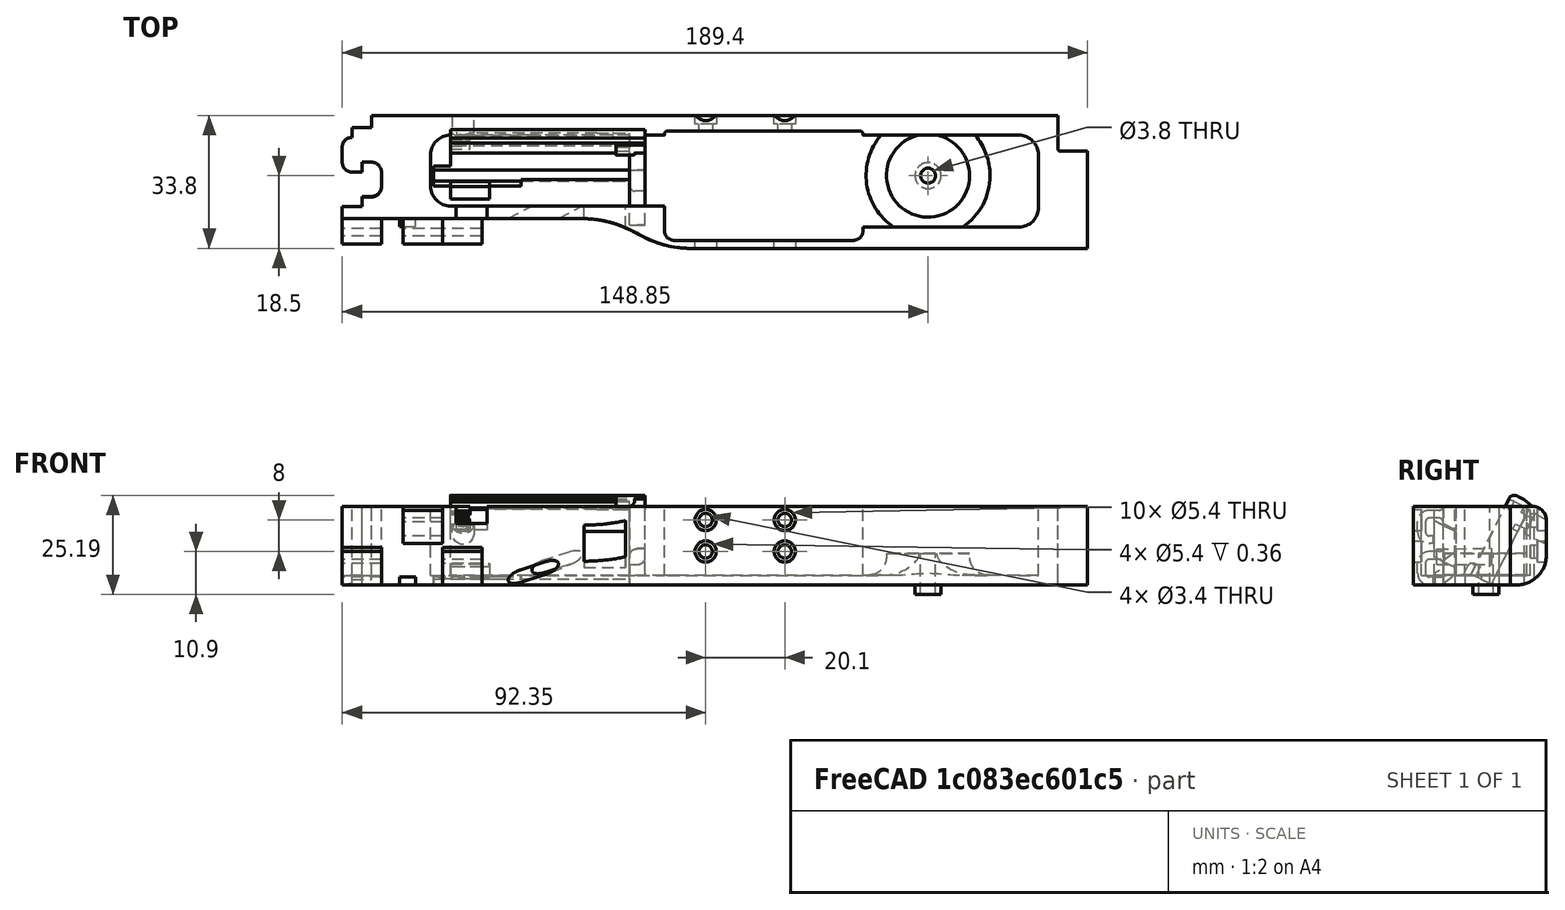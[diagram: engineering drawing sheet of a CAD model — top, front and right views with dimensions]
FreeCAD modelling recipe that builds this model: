
FCSTD DOCUMENT  (FreeCAD 0.19R0.19.2)
Label: v0_9993
License: All rights reserved
LicenseURL: http://en.wikipedia.org/wiki/All_rights_reserved
objects: Sketcher::SketchObject×44, Part::Extrusion×35, Part::MultiFuse×21, Part::Box×16, Part::Cut×15, Part::Fillet×13, App::MeasureDistance×6, Part::Cylinder×4, Part::Revolution×1, Mesh::Feature×1
note: 149 computed .brp shape members not serialized (recipe doc carries the construction recipe); baked Part::Feature solids carry a one-line shape summary decoded from their .brp

FEATURE [Sketcher::SketchObject] Sketch
  FullyConstrained = true
  sketch-geometry (36):
    g0: LineSegment StartX=0 StartY=0 StartZ=0 EndX=154.4 EndY=0 EndZ=0
    g1: LineSegment StartX=154.4 StartY=0 StartZ=0 EndX=154.4 EndY=-7.6 EndZ=0
    g2: LineSegment StartX=32.5209 StartY=-26.2 StartZ=0 EndX=-7.5 EndY=-26.2 EndZ=0
    g3-g7: Circle x5 (B-spline internal-alignment scaffolding for g8; pole/knot coordinates omitted)
    g8: BSplineCurve PolesCount=5 KnotsCount=3 Degree=3 IsPeriodic=0
    g9: GeomPoint X=61.85 Y=-33.8 Z=0
    g10: GeomPoint X=47.185 Y=-29.9 Z=0
    g11: GeomPoint X=32.5209 Y=-26.2 Z=0
    g12: Circle CenterX=121.35 CenterY=-14.3 CenterZ=0 NormalX=0 NormalY=0 NormalZ=1 AngleXU=0 Radius=3.25
    g13: LineSegment StartX=-7.5 StartY=-26.2 StartZ=0 EndX=-27.5 EndY=-26.2 EndZ=0
    g14: LineSegment StartX=-20 StartY=0 StartZ=0 EndX=0 EndY=0 EndZ=0
    g15: LineSegment StartX=-25 StartY=-3.1 StartZ=0 EndX=-20 EndY=-3.1 EndZ=0
    g16: LineSegment StartX=-25 StartY=-3.1 StartZ=0 EndX=-25 EndY=-5.6 EndZ=0
    g17: LineSegment StartX=-27.5 StartY=-8.1 StartZ=0 EndX=-27.5 EndY=-11.85 EndZ=0
    g18: ArcOfCircle CenterX=-25 CenterY=-8.1 CenterZ=0 NormalX=0 NormalY=0 NormalZ=1 AngleXU=0 Radius=2.5 StartAngle=1.5708 EndAngle=3.14159
    g19: LineSegment StartX=-25 StartY=-14.35 StartZ=0 EndX=-22.5 EndY=-14.35 EndZ=0
    g20: ArcOfCircle CenterX=-25 CenterY=-11.85 CenterZ=0 NormalX=0 NormalY=0 NormalZ=1 AngleXU=0 Radius=2.5 StartAngle=3.14159 EndAngle=4.71239
    g21: LineSegment StartX=-22.5 StartY=-14.35 StartZ=0 EndX=-22.5 EndY=-11.85 EndZ=0
    g22: LineSegment StartX=-22.5 StartY=-11.85 StartZ=0 EndX=-20 EndY=-11.85 EndZ=0
    g23: ArcOfCircle CenterX=-20 CenterY=-14.35 CenterZ=0 NormalX=0 NormalY=0 NormalZ=1 AngleXU=0 Radius=2.5 StartAngle=8e-16 EndAngle=1.5708
    g24: LineSegment StartX=-17.5 StartY=-14.35 StartZ=0 EndX=-17.5 EndY=-18.1 EndZ=0
    g25: ArcOfCircle CenterX=-20 CenterY=-18.1 CenterZ=0 NormalX=0 NormalY=0 NormalZ=1 AngleXU=0 Radius=2.5 StartAngle=4.71239 EndAngle=6.28319
    g26: LineSegment StartX=-22.5 StartY=-20.6 StartZ=0 EndX=-20 EndY=-20.6 EndZ=0
    g27: LineSegment StartX=-22.5 StartY=-20.6 StartZ=0 EndX=-22.5 EndY=-23.1 EndZ=0
    g28: LineSegment StartX=-27.5 StartY=-23.1 StartZ=0 EndX=-22.5 EndY=-23.1 EndZ=0
    g29: LineSegment StartX=-20 StartY=-3.1 StartZ=0 EndX=-20 EndY=0 EndZ=0
    g30: LineSegment StartX=-27.5 StartY=-23.1 StartZ=0 EndX=-27.5 EndY=-26.2 EndZ=0
    g31: LineSegment StartX=154.4 StartY=-7.6 StartZ=0 EndX=154.4 EndY=-8.6 EndZ=0
    g32: ArcOfCircle CenterX=154.9 CenterY=-8.6 CenterZ=0 NormalX=0 NormalY=0 NormalZ=1 AngleXU=0 Radius=0.5 StartAngle=3.14159 EndAngle=4.71239
    g33: LineSegment StartX=154.9 StartY=-9.1 StartZ=0 EndX=161.9 EndY=-9.1 EndZ=0
    g34: LineSegment StartX=161.9 StartY=-9.1 StartZ=0 EndX=161.9 EndY=-33.8 EndZ=0
    g35: LineSegment StartX=161.9 StartY=-33.8 StartZ=0 EndX=61.85 EndY=-33.8 EndZ=0
  constraints (72):
    c: PointOnObject(g0,g-2)
    c: Horizontal(g0)
    c: Distance(g0) = 154.4
    c: DistanceY(g-1,g0) = 0
    c: Vertical(g1)
    c: Distance(g1) = 7.6
    c: Coincident(g1,g0)
    c: Horizontal(g2)
    c: Block(g2)
    c: Weight(g3) = 1
    c: Coincident(g8,g2)
    c: InternalAlignment(g3-g7 -> g8) x5
    c: InternalAlignment(g9,g8)
    c: InternalAlignment(g10,g8)
    c: InternalAlignment(g11,g8)
    c: Block(g12)
    c: Coincident(g13,g2)
    c: Horizontal(g13)
    c: Distance(g13) = 20
    c: Horizontal(g14)
    c: Distance(g14) = 20
    c: Coincident(g14,g0)
    c: Horizontal(g15)
    c: Vertical(g16)
    c: Coincident(g16,g15)
    c: Vertical(g17)
    c: Coincident(g18,g16)
    c: Block(g18)
    c: Coincident(g17,g18)
    c: Horizontal(g19)
    c: Coincident(g20,g17)
    c: Block(g20)
    c: Block(g19)
    c: Vertical(g21)
    c: Coincident(g21,g19)
    c: Horizontal(g22)
    c: Coincident(g22,g21)
    c: Coincident(g23,g22)
    c: Vertical(g24)
    c: Block(g23)
    c: Coincident(g24,g23)
    c: Coincident(g25,g24)
    c: Block(g25)
    c: Horizontal(g26)
    c: Coincident(g26,g25)
    c: Vertical(g27)
    c: Coincident(g27,g26)
    c: Horizontal(g28)
    c: Coincident(g28,g27)
    c: Block(g15)
    c: Block(g28)
    c: Coincident(g29,g15)
    c: Coincident(g29,g14)
    c: Vertical(g29)
    c: Coincident(g30,g28)
    c: Coincident(g30,g13)
    c: Vertical(g30)
    c: Vertical(g31)
    c: Distance(g31) = 1
    c: Coincident(g31,g1)
    c: Coincident(g32,g31)
    c: Block(g32)
    c: Coincident(g33,g32)
    c: Horizontal(g33)
    c: Coincident(g34,g33)
    c: Vertical(g34)
    c: Block(g34)
    c: Coincident(g35,g34)
    c: Horizontal(g35)
    c: Block(g35)
    c: Coincident(g8,g35)
    c: Block(g8)
FEATURE [Part::Extrusion] Extrude  label="mainBodyBaseExtrude"
  Base = -> Sketch
  Dir = (0,0,1)
  DirMode = 2
  FaceMakerClass = Part::FaceMakerBullseye
  LengthFwd = 2.4
  LengthRev = 0
  Solid = true
  Symmetric = false
FEATURE [Sketcher::SketchObject] Sketch001
  FullyConstrained = true
  sketch-geometry (75):
    g0: ArcOfCircle CenterX=144.4 CenterY=-10 CenterZ=0 NormalX=0 NormalY=0 NormalZ=1 AngleXU=0 Radius=5 StartAngle=4.345e-13 EndAngle=1.5708
    g1: LineSegment StartX=32.5209 StartY=-26.2 StartZ=0 EndX=-7.49911 EndY=-26.2 EndZ=0
    g2: LineSegment StartX=0 StartY=0 StartZ=0 EndX=154.4 EndY=0 EndZ=0
    g3-g7: Circle x5 (B-spline internal-alignment scaffolding for g8; pole/knot coordinates omitted)
    g8: BSplineCurve PolesCount=5 KnotsCount=3 Degree=3 IsPeriodic=0
    g9: GeomPoint X=61.85 Y=-33.8 Z=0
    g10: GeomPoint X=47.1857 Y=-29.9 Z=0
    g11: GeomPoint X=32.5209 Y=-26.2 Z=0
    g12: LineSegment StartX=154.4 StartY=0 StartZ=0 EndX=154.4 EndY=-7.6 EndZ=0
    g13: LineSegment StartX=20 StartY=-5 StartZ=0 EndX=54.35 EndY=-5 EndZ=0
    g14: LineSegment StartX=104.85 StartY=-5 StartZ=0 EndX=144.4 EndY=-5 EndZ=0
    g15: LineSegment StartX=54.35 StartY=-23 StartZ=0 EndX=20 EndY=-23 EndZ=0
    g16: LineSegment StartX=-27.4991 StartY=-26.2 StartZ=0 EndX=-7.49911 EndY=-26.2 EndZ=0
    g17: LineSegment StartX=-20 StartY=0 StartZ=0 EndX=0 EndY=0 EndZ=0
    g18: LineSegment StartX=-27.4991 StartY=-23.2 StartZ=0 EndX=-22.5 EndY=-23.2 EndZ=0
    g19: LineSegment StartX=-22.5 StartY=-20.7 StartZ=0 EndX=-22.5 EndY=-23.2 EndZ=0
    g20: LineSegment StartX=-22.5 StartY=-20.7 StartZ=0 EndX=-20 EndY=-20.7 EndZ=0
    g21: ArcOfCircle CenterX=-20 CenterY=-18.2 CenterZ=0 NormalX=0 NormalY=0 NormalZ=1 AngleXU=0 Radius=2.5 StartAngle=4.71239 EndAngle=6.28319
    g22: LineSegment StartX=-17.5 StartY=-14.4 StartZ=0 EndX=-17.5 EndY=-18.2 EndZ=0
    g23: ArcOfCircle CenterX=-20 CenterY=-14.4 CenterZ=0 NormalX=0 NormalY=0 NormalZ=1 AngleXU=0 Radius=2.5 StartAngle=9e-16 EndAngle=1.5708
    g24: LineSegment StartX=-22.5 StartY=-11.9 StartZ=0 EndX=-20 EndY=-11.9 EndZ=0
    g25: LineSegment StartX=-22.5 StartY=-14.4 StartZ=0 EndX=-22.5 EndY=-11.9 EndZ=0
    g26: LineSegment StartX=-25 StartY=-14.4 StartZ=0 EndX=-22.5 EndY=-14.4 EndZ=0
    g27: ArcOfCircle CenterX=-25 CenterY=-11.9 CenterZ=0 NormalX=0 NormalY=0 NormalZ=1 AngleXU=0 Radius=2.5 StartAngle=3.14159 EndAngle=4.71239
    g28: LineSegment StartX=-27.5 StartY=-8.1 StartZ=0 EndX=-27.5 EndY=-11.9 EndZ=0
    g29: ArcOfCircle CenterX=-25 CenterY=-8.1 CenterZ=0 NormalX=0 NormalY=0 NormalZ=1 AngleXU=0 Radius=2.5 StartAngle=1.5708 EndAngle=3.14159
    g30: LineSegment StartX=-25 StartY=-3.1 StartZ=0 EndX=-25 EndY=-5.6 EndZ=0
    g31: LineSegment StartX=-20 StartY=-3.1 StartZ=0 EndX=-25 EndY=-3.1 EndZ=0
    g32: LineSegment StartX=-20 StartY=0 StartZ=0 EndX=-20 EndY=-3.1 EndZ=0
    g33: LineSegment StartX=-27.4991 StartY=-26.2 StartZ=0 EndX=-27.4991 EndY=-23.2 EndZ=0
    g34: LineSegment StartX=4.09e-14 StartY=-5 StartZ=0 EndX=20 EndY=-5 EndZ=0
    g35: ArcOfCircle CenterX=7.1e-15 CenterY=-18 CenterZ=0 NormalX=0 NormalY=0 NormalZ=1 AngleXU=0 Radius=5 StartAngle=3.14159 EndAngle=4.71239
    g36: ArcOfCircle CenterX=4.26e-14 CenterY=-10 CenterZ=0 NormalX=0 NormalY=0 NormalZ=1 AngleXU=0 Radius=5 StartAngle=1.5708 EndAngle=3.14159
    g37: LineSegment StartX=-5 StartY=-18 StartZ=0 EndX=-5 EndY=-10 EndZ=0
    g38: LineSegment StartX=6.2e-15 StartY=-23 StartZ=0 EndX=20 EndY=-23 EndZ=0
    g39: LineSegment StartX=154.4 StartY=-7.6 StartZ=0 EndX=154.4 EndY=-8.6 EndZ=0
    g40: LineSegment StartX=154.9 StartY=-9.1 StartZ=0 EndX=161.9 EndY=-9.1 EndZ=0
    g41: ArcOfCircle CenterX=154.9 CenterY=-8.6 CenterZ=0 NormalX=0 NormalY=0 NormalZ=1 AngleXU=0 Radius=0.5 StartAngle=3.14159 EndAngle=4.71299
    g42: LineSegment StartX=104.85 StartY=-28.3916 StartZ=0 EndX=144.408 EndY=-28.3916 EndZ=0
    g43: LineSegment StartX=149.4 StartY=-10 StartZ=0 EndX=149.4 EndY=-23.4 EndZ=0
    g44: ArcOfCircle CenterX=144.408 CenterY=-23.4 CenterZ=0 NormalX=0 NormalY=0 NormalZ=1 AngleXU=0 Radius=4.99164 StartAngle=4.71239 EndAngle=6.28319
    g45: LineSegment StartX=104.85 StartY=-28.3916 StartZ=0 EndX=104.85 EndY=-28.7833 EndZ=0
    g46: LineSegment StartX=54.35 StartY=-28.7916 StartZ=0 EndX=54.35 EndY=-23 EndZ=0
    g47: LineSegment StartX=161.9 StartY=-33.8 StartZ=0 EndX=161.9 EndY=-9.1 EndZ=0
    g48: LineSegment StartX=61.85 StartY=-33.8 StartZ=0 EndX=161.9 EndY=-33.8 EndZ=0
    g49: Circle CenterX=54.35 CenterY=-28.7916 CenterZ=0 NormalX=0 NormalY=0 NormalZ=1 AngleXU=0 Radius=1
    g50: Circle CenterX=54.35 CenterY=-31.7916 CenterZ=0 NormalX=0 NormalY=0 NormalZ=1 AngleXU=0 Radius=1
    g51: Circle CenterX=57.35 CenterY=-31.7916 CenterZ=0 NormalX=0 NormalY=0 NormalZ=1 AngleXU=0 Radius=1
    g52: BSplineCurve PolesCount=3 KnotsCount=2 Degree=2 IsPeriodic=0
    g53: GeomPoint X=54.35 Y=-28.7916 Z=0
    g54: GeomPoint X=57.35 Y=-31.7916 Z=0
    g55: Circle CenterX=104.85 CenterY=-28.7833 CenterZ=0 NormalX=0 NormalY=0 NormalZ=1 AngleXU=0 Radius=1
    g56: Circle CenterX=104.85 CenterY=-31.7916 CenterZ=0 NormalX=0 NormalY=0 NormalZ=1 AngleXU=0 Radius=1
    g57: Circle CenterX=101.85 CenterY=-31.7916 CenterZ=0 NormalX=0 NormalY=0 NormalZ=1 AngleXU=0 Radius=1
    g58: BSplineCurve PolesCount=3 KnotsCount=2 Degree=2 IsPeriodic=0
    g59: GeomPoint X=104.85 Y=-28.7833 Z=0
    g60: GeomPoint X=101.85 Y=-31.7916 Z=0
    g61: LineSegment StartX=57.35 StartY=-31.7916 StartZ=0 EndX=101.85 EndY=-31.7916 EndZ=0
    g62: Circle CenterX=54.35 CenterY=-5 CenterZ=0 NormalX=0 NormalY=0 NormalZ=1 AngleXU=0 Radius=1
    g63: Circle CenterX=54.35 CenterY=-4 CenterZ=0 NormalX=0 NormalY=0 NormalZ=1 AngleXU=0 Radius=1
    g64: Circle CenterX=55.15 CenterY=-4 CenterZ=0 NormalX=0 NormalY=0 NormalZ=1 AngleXU=0 Radius=1
    g65: BSplineCurve PolesCount=3 KnotsCount=2 Degree=2 IsPeriodic=0
    g66: GeomPoint X=54.35 Y=-5 Z=0
    g67: GeomPoint X=55.15 Y=-4 Z=0
    g68: Circle CenterX=104.85 CenterY=-5 CenterZ=0 NormalX=0 NormalY=0 NormalZ=1 AngleXU=0 Radius=1
    g69: Circle CenterX=104.85 CenterY=-4 CenterZ=0 NormalX=0 NormalY=0 NormalZ=1 AngleXU=0 Radius=1
    g70: Circle CenterX=104.05 CenterY=-4 CenterZ=0 NormalX=0 NormalY=0 NormalZ=1 AngleXU=0 Radius=1
    g71: BSplineCurve PolesCount=3 KnotsCount=2 Degree=2 IsPeriodic=0
    g72: GeomPoint X=104.85 Y=-5 Z=0
    g73: GeomPoint X=104.05 Y=-4 Z=0
    g74: LineSegment StartX=104.05 StartY=-4 StartZ=0 EndX=55.15 EndY=-4 EndZ=0
  constraints (156):
    c: PointOnObject(g2,g-2)
    c: DistanceY(g-1,g2) = 0
    c: Block(g0)
    c: Horizontal(g1)
    c: Distance(g1) = 40.02
    c: Horizontal(g2)
    c: Block(g2)
    c: Weight(g3) = 1
    c: Equal(g3, g4-g7) x4
    c: Coincident(g8,g1)
    c: InternalAlignment(g3-g7 -> g8) x5
    c: InternalAlignment(g9,g8)
    c: InternalAlignment(g10,g8)
    c: InternalAlignment(g11,g8)
    c: Vertical(g12)
    c: Coincident(g12,g2)
    c: Distance(g12) = 7.6
    c: Block(g12)
    c: Horizontal(g13)
    c: Coincident(g14,g0)
    c: Horizontal(g14)
    c: Horizontal(g15)
    c: Horizontal(g16)
    c: Distance(g16) = 20
    c: Coincident(g1,g16)
    c: Horizontal(g17)
    c: Distance(g17) = 20
    c: Coincident(g17,g2)
    c: Horizontal(g31)
    c: Vertical(g30)
    c: Coincident(g29,g30)
    c: Vertical(g28)
    c: Block(g29)
    c: Coincident(g27,g28)
    c: Block(g27)
    c: Horizontal(g26)
    c: Coincident(g26,g27)
    c: Vertical(g25)
    c: Coincident(g25,g26)
    c: Horizontal(g24)
    c: Coincident(g23,g24)
    c: Block(g23)
    c: Vertical(g22)
    c: Coincident(g21,g22)
    c: Block(g21)
    c: Horizontal(g20)
    c: Coincident(g20,g21)
    c: Vertical(g19)
    c: Coincident(g19,g20)
    c: Horizontal(g18)
    c: Coincident(g18,g19)
    c: Coincident(g32,g17)
    c: Coincident(g32,g31)
    c: Vertical(g32)
    c: Coincident(g33,g16)
    c: Coincident(g33,g18)
    c: Vertical(g33)
    c: Block(g33)
    c: Block(g18)
    c: Block(g22)
    c: Block(g26)
    c: Block(g25)
    c: Block(g24)
    c: Block(g28)
    c: Block(g31)
    c: Block(g30)
    c: Horizontal(g34)
    c: Distance(g34) = 20
    c: Block(g35)
    c: Block(g36)
    c: Coincident(g37,g35)
    c: Coincident(g37,g36)
    c: Vertical(g37)
    c: Coincident(g38,g35)
    c: Coincident(g38,g15)
    c: Horizontal(g38)
    c: Block(g38)
    c: Block(g34)
    c: Block(g13)
    c: Vertical(g39)
    c: Distance(g39) = 1
    c: Coincident(g39,g12)
    c: Horizontal(g40)
    c: Coincident(g41,g39)
    c: Coincident(g41,g40)
    c: Block(g39)
    c: Block(g41)
    c: Horizontal(g42)
    c: Vertical(g43)
    c: Distance(g43) = 13.4
    c: Coincident(g43,g0)
    c: Block(g42)
    c: Block(g43)
    c: Coincident(g44,g43)
    c: Coincident(g44,g42)
    c: Block(g44)
    c: Distance(g15) = 34.35
    c: Coincident(g45,g42)
    c: Vertical(g45)
    c: Coincident(g46,g15)
    c: Vertical(g46)
    c: Coincident(g47,g40)
    c: Vertical(g47)
    c: Block(g47)
    c: Coincident(g48,g47)
    c: Horizontal(g48)
    c: Block(g48)
    c: Coincident(g8,g48)
    c: Block(g8)
    c: Coincident(g52,g46)
    c: Weight(g49) = 1
    c: Equal(g49,g50)
    c: Equal(g49,g51)
    c: InternalAlignment(g49,g52)
    c: InternalAlignment(g50,g52)
    c: InternalAlignment(g51,g52)
    c: InternalAlignment(g53,g52)
    c: InternalAlignment(g54,g52)
    c: Coincident(g58,g45)
    c: Weight(g55) = 1
    c: Equal(g55,g56)
    c: Equal(g55,g57)
    c: InternalAlignment(g55,g58)
    c: InternalAlignment(g56,g58)
    c: InternalAlignment(g57,g58)
    c: InternalAlignment(g59,g58)
    c: InternalAlignment(g60,g58)
    c: Block(g58)
    c: Block(g52)
    c: Coincident(g61,g52)
    c: Coincident(g61,g58)
    c: Horizontal(g61)
    c: Block(g14)
    c: Coincident(g65,g13)
    c: Weight(g62) = 1
    c: Equal(g62,g63)
    c: Equal(g62,g64)
    c: InternalAlignment(g62,g65)
    c: InternalAlignment(g63,g65)
    c: InternalAlignment(g64,g65)
    c: InternalAlignment(g66,g65)
    c: InternalAlignment(g67,g65)
    c: Block(g65)
    c: Coincident(g71,g14)
    c: Weight(g68) = 1
    c: Equal(g68,g69)
    c: Equal(g68,g70)
    c: InternalAlignment(g68,g71)
    c: InternalAlignment(g69,g71)
    c: InternalAlignment(g70,g71)
    c: InternalAlignment(g72,g71)
    c: InternalAlignment(g73,g71)
    c: Block(g71)
    c: Coincident(g74,g71)
    c: Coincident(g74,g65)
    c: Horizontal(g74)
FEATURE [Sketcher::SketchObject] Sketch005
  FullyConstrained = true
  Placement = pos=(0,0,0) rot=(1,0,0;1.5708rad)
  sketch-geometry (4):
    g0: Circle CenterX=84.95 CenterY=16.5 CenterZ=0 NormalX=0 NormalY=0 NormalZ=1 AngleXU=0 Radius=1.7
    g1: Circle CenterX=84.95 CenterY=8.5 CenterZ=0 NormalX=0 NormalY=0 NormalZ=1 AngleXU=0 Radius=1.7
    g2: Circle CenterX=64.85 CenterY=8.5 CenterZ=0 NormalX=0 NormalY=0 NormalZ=1 AngleXU=0 Radius=1.7
    g3: Circle CenterX=64.85 CenterY=16.5 CenterZ=0 NormalX=0 NormalY=0 NormalZ=1 AngleXU=0 Radius=1.7
  constraints (4):
    c: Block(g0)
    c: Block(g1)
    c: Block(g2)
    c: Block(g3)
FEATURE [Part::Extrusion] Extrude004  label="removeFromMainBodyToCreateScrewHolesForSolenoidExtrude004"
  Base = -> Sketch005
  Dir = (0,-1,1.1e-15)
  DirMode = 2
  FaceMakerClass = Part::FaceMakerBullseye
  LengthFwd = 10
  LengthRev = 0
  Solid = true
  Symmetric = false
FEATURE [Sketcher::SketchObject] Sketch004
  FullyConstrained = true
  Placement = pos=(0,0,0) rot=(1,0,0;1.5708rad)
  sketch-geometry (12):
    g0: LineSegment StartX=15.75 StartY=2.5 StartZ=0 EndX=15.75 EndY=0 EndZ=0
    g1: Circle CenterX=15.75 CenterY=2.5 CenterZ=0 NormalX=0 NormalY=0 NormalZ=1 AngleXU=0 Radius=1
    g2: Circle CenterX=10.55 CenterY=2.5 CenterZ=0 NormalX=0 NormalY=0 NormalZ=1 AngleXU=0 Radius=1
    g3: Circle CenterX=10.55 CenterY=8 CenterZ=0 NormalX=0 NormalY=0 NormalZ=1 AngleXU=0 Radius=1
    g4: BSplineCurve PolesCount=3 KnotsCount=2 Degree=2 IsPeriodic=0
    g5: GeomPoint X=15.75 Y=2.5 Z=0
    g6: GeomPoint X=10.55 Y=8 Z=0
    g7: LineSegment StartX=1.9 StartY=8 StartZ=0 EndX=10.55 EndY=8 EndZ=0
    g8: LineSegment StartX=1.9 StartY=-2.4 StartZ=0 EndX=1.9 EndY=8 EndZ=0
    g9: LineSegment StartX=3.30092 StartY=-2.4 StartZ=0 EndX=3.30092 EndY=0 EndZ=0
    g10: LineSegment StartX=15.75 StartY=0 StartZ=0 EndX=3.30092 EndY=0 EndZ=0
    g11: LineSegment StartX=3.30092 StartY=-2.4 StartZ=0 EndX=1.9 EndY=-2.4 EndZ=0
  constraints (26):
    c: Vertical(g0)
    c: Distance(g0) = 2.5
    c: Coincident(g4,g0)
    c: Weight(g1) = 1
    c: Equal(g1,g2)
    c: Equal(g1,g3)
    c: InternalAlignment(g1,g4)
    c: InternalAlignment(g2,g4)
    c: InternalAlignment(g3,g4)
    c: InternalAlignment(g5,g4)
    c: InternalAlignment(g6,g4)
    c: Block(g4)
    c: Coincident(g7,g4)
    c: Horizontal(g7)
    c: Vertical(g8)
    c: Coincident(g8,g7)
    c: Block(g8)
    c: Vertical(g9)
    c: Coincident(g10,g0)
    c: PointOnObject(g10,g-1)
    c: Horizontal(g10)
    c: Coincident(g10,g9)
    c: Block(g9)
    c: Coincident(g11,g9)
    c: Coincident(g11,g8)
    c: Horizontal(g11)
FEATURE [Sketcher::SketchObject] Sketch007
  FullyConstrained = true
  Placement = pos=(0,-14.3,2.37) rot=(-1,0,0;2.03453rad)
  sketch-geometry (6):
    g0: LineSegment StartX=0 StartY=0 StartZ=0 EndX=45.5 EndY=0 EndZ=0
    g1: LineSegment StartX=0 StartY=0 StartZ=0 EndX=0 EndY=-21.2 EndZ=0
    g2: LineSegment StartX=45.5 StartY=0 StartZ=0 EndX=49.5 EndY=0 EndZ=0
    g3: LineSegment StartX=49.5 StartY=0 StartZ=0 EndX=49.5 EndY=-21.2 EndZ=0
    g4: LineSegment StartX=49.5 StartY=-21.2 StartZ=0 EndX=0 EndY=-21.2 EndZ=0
    g5: Circle CenterX=3.25 CenterY=-18.05 CenterZ=0 NormalX=0 NormalY=0 NormalZ=1 AngleXU=0 Radius=1.6
  constraints (15):
    c: Coincident(g0,g-1)
    c: Horizontal(g0)
    c: Distance(g0) = 45.5
    c: Coincident(g1,g0)
    c: Vertical(g1)
    c: Horizontal(g2)
    c: Distance(g2) = 4
    c: Coincident(g2,g0)
    c: Coincident(g3,g2)
    c: Vertical(g3)
    c: Block(g3)
    c: Coincident(g4,g3)
    c: Horizontal(g4)
    c: Coincident(g4,g1)
    c: Block(g5)
FEATURE [Part::Extrusion] Extrude005  label="solenoidDriverHolderExtrude005"
  Base = -> Sketch007
  Dir = (0,0.894389,-0.447291)
  DirMode = 2
  FaceMakerClass = Part::FaceMakerBullseye
  LengthFwd = 10
  LengthRev = 0
  Placement = pos=(0,0,-2) rot=(0,0,1;0rad)
  Solid = true
  Symmetric = false
FEATURE [Sketcher::SketchObject] Sketch008
  FullyConstrained = false
  Placement = pos=(0,-4.3,-2.6) rot=(-1,0,0;2.03453rad)
  sketch-geometry (1):
    g0: Circle CenterX=42.25 CenterY=-3.15 CenterZ=0 NormalX=0 NormalY=0 NormalZ=1 AngleXU=0 Radius=4.5
FEATURE [Sketcher::SketchObject] Sketch009
  FullyConstrained = true
  Placement = pos=(0,-4.3,-2.6) rot=(-1,0,0;2.03453rad)
  sketch-geometry (1):
    g0: Circle CenterX=3.25 CenterY=-18.0217 CenterZ=0 NormalX=0 NormalY=0 NormalZ=1 AngleXU=0 Radius=2.8
  constraints (1):
    c: Block(g0)
FEATURE [Sketcher::SketchObject] Sketch010
  FullyConstrained = true
  Placement = pos=(0,-14.3,2.37) rot=(-1,0,0;2.03453rad)
  sketch-geometry (1):
    g0: Circle CenterX=3.25 CenterY=-18.05 CenterZ=0 NormalX=0 NormalY=0 NormalZ=1 AngleXU=0 Radius=1.6
  constraints (1):
    c: Block(g0)
FEATURE [Part::Extrusion] Extrude008  label="removeFromScrewHole3"
  Base = -> Sketch010
  Dir = (0,0.894389,-0.447291)
  DirMode = 2
  FaceMakerClass = Part::FaceMakerBullseye
  LengthFwd = -25
  LengthRev = 0
  Placement = pos=(0,4,-4) rot=(0,0,1;0rad)
  Solid = true
  Symmetric = false
FEATURE [Sketcher::SketchObject] Sketch011
  FullyConstrained = true
  Placement = pos=(0,-14.3,2.37) rot=(-1,0,0;2.03453rad)
  sketch-geometry (4):
    g0: LineSegment StartX=49.5 StartY=-21.2 StartZ=0 EndX=49.5 EndY=-22.8 EndZ=0
    g1: LineSegment StartX=49.5 StartY=-22.8 StartZ=0 EndX=0.002238 EndY=-22.8 EndZ=0
    g2: LineSegment StartX=0.002238 StartY=-21.2 StartZ=0 EndX=0.002238 EndY=-22.8 EndZ=0
    g3: LineSegment StartX=49.5 StartY=-21.2 StartZ=0 EndX=0.002238 EndY=-21.2 EndZ=0
  constraints (10):
    c: Vertical(g0)
    c: Distance(g0) = 1.6
    c: Coincident(g1,g0)
    c: Horizontal(g1)
    c: Vertical(g2)
    c: Coincident(g2,g1)
    c: Coincident(g3,g0)
    c: Coincident(g3,g2)
    c: Horizontal(g3)
    c: Block(g3)
FEATURE [Part::Extrusion] Extrude009  label="solenoidDriverTopLipFront"
  Base = -> Sketch011
  Dir = (0,0.894389,-0.447291)
  DirMode = 2
  FaceMakerClass = Part::FaceMakerBullseye
  LengthFwd = -2
  LengthRev = 0
  Placement = pos=(0,-2.9,-0.35) rot=(0,0,1;0rad)
  Solid = true
  Symmetric = false
FEATURE [Sketcher::SketchObject] Sketch012
  FullyConstrained = true
  Placement = pos=(0,-14.3,2.37) rot=(-1,0,0;2.03453rad)
  sketch-geometry (4):
    g0: LineSegment StartX=49.5 StartY=-21.2 StartZ=0 EndX=49.5 EndY=-22.8 EndZ=0
    g1: LineSegment StartX=49.5 StartY=-22.8 StartZ=0 EndX=0.002238 EndY=-22.8 EndZ=0
    g2: LineSegment StartX=0.002238 StartY=-21.2 StartZ=0 EndX=0.002238 EndY=-22.8 EndZ=0
    g3: LineSegment StartX=49.5 StartY=-21.2 StartZ=0 EndX=0.002238 EndY=-21.2 EndZ=0
  constraints (10):
    c: Vertical(g0)
    c: Distance(g0) = 1.6
    c: Coincident(g1,g0)
    c: Horizontal(g1)
    c: Vertical(g2)
    c: Coincident(g2,g1)
    c: Coincident(g3,g0)
    c: Coincident(g3,g2)
    c: Horizontal(g3)
    c: Block(g3)
FEATURE [Part::Extrusion] Extrude010  label="solenoidDriverTopLipLowerExtrude010"
  Base = -> Sketch012
  Dir = (0,0.894389,-0.447291)
  DirMode = 2
  FaceMakerClass = Part::FaceMakerBullseye
  LengthFwd = 5.05
  LengthRev = 0
  Solid = true
  Symmetric = false
FEATURE [Sketcher::SketchObject] Sketch015
  FullyConstrained = true
  Placement = pos=(0,-14.3,2.37) rot=(-1,0,0;2.03453rad)
  sketch-geometry (4):
    g0: LineSegment StartX=0 StartY=1.5 StartZ=0 EndX=0 EndY=0 EndZ=0
    g1: LineSegment StartX=0 StartY=1.5 StartZ=0 EndX=5 EndY=1.5 EndZ=0
    g2: LineSegment StartX=5 StartY=1.5 StartZ=0 EndX=5 EndY=0 EndZ=0
    g3: LineSegment StartX=0 StartY=0 StartZ=0 EndX=5 EndY=0 EndZ=0
  constraints (13):
    c: Vertical(g0)
    c: Distance(g0) = 1.5
    c: Horizontal(g1)
    c: Distance(g1) = 5
    c: Coincident(g1,g0)
    c: Vertical(g2)
    c: Distance(g2) = 1.5
    c: Coincident(g2,g1)
    c: Block(g1)
    c: Block(g2)
    c: Block(g0)
    c: Coincident(g3,g0)
    c: Coincident(g3,g2)
FEATURE [Part::Extrusion] Extrude013  label="solenoidDriverBottomLipTopExtrude012"
  Base = -> Sketch015
  Dir = (0,0.894389,-0.447291)
  DirMode = 2
  FaceMakerClass = Part::FaceMakerBullseye
  LengthFwd = -6.5
  LengthRev = 0
  Placement = pos=(0,-14.15,19.65) rot=(1,0,0;1.5708rad)
  Solid = true
  Symmetric = false
FEATURE [Sketcher::SketchObject] Sketch016
  FullyConstrained = true
  Placement = pos=(0,0,0) rot=(1,0,0;1.5708rad)
  sketch-geometry (4):
    g0: Circle CenterX=84.15 CenterY=16.5 CenterZ=0 NormalX=0 NormalY=0 NormalZ=1 AngleXU=0 Radius=2.7
    g1: Circle CenterX=64.05 CenterY=16.5 CenterZ=0 NormalX=0 NormalY=0 NormalZ=1 AngleXU=0 Radius=2.7
    g2: Circle CenterX=64.05 CenterY=8.5 CenterZ=0 NormalX=0 NormalY=0 NormalZ=1 AngleXU=0 Radius=2.7
    g3: Circle CenterX=84.15 CenterY=8.5 CenterZ=0 NormalX=0 NormalY=0 NormalZ=1 AngleXU=0 Radius=2.7
  constraints (4):
    c: Block(g0)
    c: Block(g1)
    c: Block(g3)
    c: Block(g2)
FEATURE [Part::Extrusion] Extrude014  label="removeFromMainBodyToCreateScrewHoleCounterSinks"
  Base = -> Sketch016
  Dir = (0,-1,1.1e-15)
  DirMode = 2
  FaceMakerClass = Part::FaceMakerBullseye
  LengthFwd = 1.9
  LengthRev = 0
  Placement = pos=(0.8,-0.36,0) rot=(0,0,1;0rad)
  Solid = true
  Symmetric = false
FEATURE [Part::Extrusion] Extrude015  label="removeFromScrewHole2Extrude007"
  Base = -> Sketch009
  Dir = (0,0.894389,-0.447291)
  DirMode = 2
  FaceMakerClass = Part::FaceMakerBullseye
  LengthFwd = 10
  LengthRev = 0
  Placement = pos=(0,-8,2) rot=(0,0,1;0rad)
  Solid = true
  Symmetric = false
FEATURE [Sketcher::SketchObject] Sketch017
  FullyConstrained = true
  Placement = pos=(0,-14.3,2.37) rot=(-1,0,0;2.03453rad)
  sketch-geometry (4):
    g0: LineSegment StartX=0 StartY=1.5 StartZ=0 EndX=0 EndY=0 EndZ=0
    g1: LineSegment StartX=0 StartY=1.5 StartZ=0 EndX=5 EndY=1.5 EndZ=0
    g2: LineSegment StartX=5 StartY=1.5 StartZ=0 EndX=5 EndY=0 EndZ=0
    g3: LineSegment StartX=0 StartY=0 StartZ=0 EndX=5 EndY=0 EndZ=0
  constraints (13):
    c: Vertical(g0)
    c: Distance(g0) = 1.5
    c: Horizontal(g1)
    c: Distance(g1) = 5
    c: Coincident(g1,g0)
    c: Vertical(g2)
    c: Distance(g2) = 1.5
    c: Coincident(g2,g1)
    c: Block(g1)
    c: Block(g2)
    c: Block(g0)
    c: Coincident(g3,g0)
    c: Coincident(g3,g2)
FEATURE [Part::Extrusion] Extrude016  label="solenoidDriverBottomLipTopExtrude013"
  Base = -> Sketch017
  Dir = (0,0.894389,-0.447291)
  DirMode = 2
  FaceMakerClass = Part::FaceMakerBullseye
  LengthFwd = -6.5
  LengthRev = 0
  Placement = pos=(0,-15.45,20.3) rot=(1,0,0;1.5708rad)
  Solid = true
  Symmetric = false
FEATURE [Part::Fillet] Fillet005  label="solenoidDriverBottomLipTopFillet005"
  Base = -> Extrude016
  Edges = 1 edges r=1.4: [Edge6]
FEATURE [Sketcher::SketchObject] Sketch018
  FullyConstrained = true
  Placement = pos=(38.5,-14.3,2.37) rot=(-1,0,0;2.03453rad)
  sketch-geometry (4):
    g0: LineSegment StartX=11 StartY=0 StartZ=0 EndX=11 EndY=1.5 EndZ=0
    g1: LineSegment StartX=11 StartY=0 StartZ=0 EndX=3.6 EndY=0 EndZ=0
    g2: LineSegment StartX=3.6 StartY=0 StartZ=0 EndX=3.6 EndY=1.5 EndZ=0
    g3: LineSegment StartX=11 StartY=1.5 StartZ=0 EndX=3.6 EndY=1.5 EndZ=0
  constraints (12):
    c: PointOnObject(g0,g-1)
    c: Vertical(g0)
    c: Distance(g0) = 1.5
    c: Horizontal(g1)
    c: Distance(g1) = 7.4
    c: Coincident(g1,g0)
    c: Block(g0)
    c: Coincident(g2,g1)
    c: Vertical(g2)
    c: Coincident(g3,g0)
    c: Horizontal(g3)
    c: Coincident(g2,g3)
FEATURE [Part::Extrusion] Extrude017
  Base = -> Sketch018
  Dir = (0,0.894389,-0.447291)
  DirMode = 2
  FaceMakerClass = Part::FaceMakerBullseye
  LengthFwd = 4
  LengthRev = 0
  Placement = pos=(0,-8.212,34.025) rot=(1,0,0;1.5708rad)
  Solid = true
  Symmetric = false
FEATURE [Sketcher::SketchObject] Sketch019
  FullyConstrained = true
  Placement = pos=(0,0,0) rot=(1,0,0;1.5708rad)
  sketch-geometry (4):
    g0: Circle CenterX=84.95 CenterY=8.5 CenterZ=0 NormalX=0 NormalY=0 NormalZ=1 AngleXU=0 Radius=2.7
    g1: Circle CenterX=64.85 CenterY=8.5 CenterZ=0 NormalX=0 NormalY=0 NormalZ=1 AngleXU=0 Radius=2.7
    g2: Circle CenterX=64.85 CenterY=16.5 CenterZ=0 NormalX=0 NormalY=0 NormalZ=1 AngleXU=0 Radius=2.7
    g3: Circle CenterX=84.95 CenterY=16.5 CenterZ=0 NormalX=0 NormalY=0 NormalZ=1 AngleXU=0 Radius=2.7
  constraints (4):
    c: Block(g3)
    c: Block(g2)
    c: Block(g0)
    c: Block(g1)
FEATURE [Part::Extrusion] Extrude019  label="removeSolenoidAdjusterHoles"
  Base = -> Sketch019
  Dir = (0,-1,1.1e-15)
  DirMode = 2
  FaceMakerClass = Part::FaceMakerBullseye
  LengthFwd = 6
  LengthRev = 0
  Placement = pos=(0,-30,0) rot=(0,0,1;0rad)
  Solid = true
  Symmetric = false
FEATURE [Sketcher::SketchObject] Sketch020
  FullyConstrained = true
  Placement = pos=(0,-14.3,2.37) rot=(-1,0,0;2.03453rad)
  sketch-geometry (6):
    g0: LineSegment StartX=45.5 StartY=-21.2 StartZ=0 EndX=49.5 EndY=-21.2 EndZ=0
    g1: LineSegment StartX=45.5 StartY=0 StartZ=0 EndX=49.5 EndY=0 EndZ=0
    g2: LineSegment StartX=49.5 StartY=0 StartZ=0 EndX=49.5 EndY=-21.2 EndZ=0
    g3: LineSegment StartX=4 StartY=0 StartZ=0 EndX=4 EndY=-21.2 EndZ=0
    g4: LineSegment StartX=45.5 StartY=-21.2 StartZ=0 EndX=4 EndY=-21.2 EndZ=0
    g5: LineSegment StartX=4 StartY=0 StartZ=0 EndX=45.5 EndY=0 EndZ=0
  constraints (16):
    c: Horizontal(g0)
    c: Distance(g0) = 4
    c: Horizontal(g1)
    c: Distance(g1) = 4
    c: Coincident(g2,g1)
    c: Coincident(g2,g0)
    c: Vertical(g2)
    c: Block(g2)
    c: Vertical(g3)
    c: Coincident(g4,g0)
    c: Horizontal(g4)
    c: Coincident(g4,g3)
    c: Coincident(g5,g1)
    c: Horizontal(g5)
    c: Block(g3)
    c: Block(g5)
FEATURE [Part::Box] Box  label="Cube"
  AttacherType = Attacher::AttachEngine3D
  Height = 10
  Length = 190
  Placement = pos=(-30,0,0) rot=(0,0,1;0rad)
  Width = 10
FEATURE [Part::Fillet] Fillet008
  Base = -> Box
  Edges = 1 edges r=7.5: [Edge11]
FEATURE [Part::Box] Box001  label="Cube001"
  AttacherType = Attacher::AttachEngine3D
  Height = 10
  Length = 190
  Placement = pos=(-35,0,0) rot=(0,0,1;0rad)
  Width = 10
FEATURE [Part::Cut] Cut  label="filletMain"
  Base = -> Box001
  Placement = pos=(0,-10,0) rot=(0,0,1;0rad)
  Tool = -> Fillet008
FEATURE [Part::Box] Box002  label="Cube002"
  AttacherType = Attacher::AttachEngine3D
  Height = 30
  Length = 190
  Placement = pos=(-20,0,0) rot=(0,0,1;0rad)
  Width = 10
FEATURE [Part::Box] Box003  label="Cube003"
  AttacherType = Attacher::AttachEngine3D
  Height = 10
  Length = 190
  Placement = pos=(-90,-50,-10) rot=(0,0,1;0rad)
  Width = 50
FEATURE [Sketcher::SketchObject] Sketch021
  FullyConstrained = true
  Placement = pos=(0,-14.3,2.37) rot=(-1,0,0;2.03453rad)
  sketch-geometry (6):
    g0: LineSegment StartX=41.65 StartY=-3.15 StartZ=0 EndX=38.95 EndY=-3.15 EndZ=0
    g1: LineSegment StartX=36.25 StartY=-3.15 StartZ=0 EndX=38.95 EndY=-3.15 EndZ=0
    g2: LineSegment StartX=41.65 StartY=-3.15 StartZ=0 EndX=41.65 EndY=-7.15 EndZ=0
    g3: LineSegment StartX=38.95 StartY=-7.15 StartZ=0 EndX=41.65 EndY=-7.15 EndZ=0
    g4: LineSegment StartX=38.95 StartY=-7.15 StartZ=0 EndX=36.25 EndY=-7.15 EndZ=0
    g5: LineSegment StartX=36.25 StartY=-3.15 StartZ=0 EndX=36.25 EndY=-7.15 EndZ=0
  constraints (16):
    c: Horizontal(g0)
    c: Distance(g0) = 2.7
    c: Horizontal(g1)
    c: Distance(g1) = 2.7
    c: Coincident(g1,g0)
    c: Block(g0)
    c: Coincident(g2,g0)
    c: Vertical(g2)
    c: Horizontal(g3)
    c: Coincident(g3,g2)
    c: Horizontal(g4)
    c: Coincident(g5,g1)
    c: Vertical(g5)
    c: Coincident(g5,g4)
    c: Block(g3)
    c: Block(g4)
FEATURE [Sketcher::SketchObject] Sketch022
  FullyConstrained = true
  Placement = pos=(0,-14.3,2.37) rot=(-1,0,0;2.03453rad)
  sketch-geometry (6):
    g0: LineSegment StartX=41.65 StartY=-3.15 StartZ=0 EndX=38.95 EndY=-3.15 EndZ=0
    g1: LineSegment StartX=36.25 StartY=-3.15 StartZ=0 EndX=38.95 EndY=-3.15 EndZ=0
    g2: LineSegment StartX=41.65 StartY=-3.15 StartZ=0 EndX=41.65 EndY=-7.15 EndZ=0
    g3: LineSegment StartX=38.95 StartY=-7.15 StartZ=0 EndX=41.65 EndY=-7.15 EndZ=0
    g4: LineSegment StartX=38.95 StartY=-7.15 StartZ=0 EndX=36.25 EndY=-7.15 EndZ=0
    g5: LineSegment StartX=36.25 StartY=-3.15 StartZ=0 EndX=36.25 EndY=-7.15 EndZ=0
  constraints (16):
    c: Horizontal(g0)
    c: Distance(g0) = 2.7
    c: Horizontal(g1)
    c: Distance(g1) = 2.7
    c: Coincident(g1,g0)
    c: Block(g0)
    c: Coincident(g2,g0)
    c: Vertical(g2)
    c: Horizontal(g3)
    c: Coincident(g3,g2)
    c: Horizontal(g4)
    c: Coincident(g5,g1)
    c: Vertical(g5)
    c: Coincident(g5,g4)
    c: Block(g3)
    c: Block(g4)
FEATURE [Sketcher::SketchObject] Sketch024
  FullyConstrained = true
  Placement = pos=(0,-14.3,2.37) rot=(-1,0,0;2.03453rad)
  sketch-geometry (4):
    g0: LineSegment StartX=49.5 StartY=-21.2 StartZ=0 EndX=49.5 EndY=-22.8 EndZ=0
    g1: LineSegment StartX=49.5 StartY=-22.8 StartZ=0 EndX=0.002238 EndY=-22.8 EndZ=0
    g2: LineSegment StartX=0.002238 StartY=-21.2 StartZ=0 EndX=0.002238 EndY=-22.8 EndZ=0
    g3: LineSegment StartX=49.5 StartY=-21.2 StartZ=0 EndX=0.002238 EndY=-21.2 EndZ=0
  constraints (10):
    c: Vertical(g0)
    c: Distance(g0) = 1.6
    c: Coincident(g1,g0)
    c: Horizontal(g1)
    c: Vertical(g2)
    c: Coincident(g2,g1)
    c: Coincident(g3,g0)
    c: Coincident(g3,g2)
    c: Horizontal(g3)
    c: Block(g3)
FEATURE [Sketcher::SketchObject] Sketch025
  FullyConstrained = true
  Placement = pos=(0,-14.3,2.37) rot=(-1,0,0;2.03453rad)
  sketch-geometry (4):
    g0: LineSegment StartX=0 StartY=1.5 StartZ=0 EndX=0 EndY=0 EndZ=0
    g1: LineSegment StartX=0 StartY=1.5 StartZ=0 EndX=5 EndY=1.5 EndZ=0
    g2: LineSegment StartX=5 StartY=1.5 StartZ=0 EndX=5 EndY=0 EndZ=0
    g3: LineSegment StartX=0 StartY=0 StartZ=0 EndX=5 EndY=0 EndZ=0
  constraints (13):
    c: Vertical(g0)
    c: Distance(g0) = 1.5
    c: Horizontal(g1)
    c: Distance(g1) = 5
    c: Coincident(g1,g0)
    c: Vertical(g2)
    c: Distance(g2) = 1.5
    c: Coincident(g2,g1)
    c: Block(g1)
    c: Block(g2)
    c: Block(g0)
    c: Coincident(g3,g0)
    c: Coincident(g3,g2)
FEATURE [Part::Extrusion] Extrude022  label="solenoidDriverBottomLipTopExtrude014"
  Base = -> Sketch025
  Dir = (0,0.894389,-0.447291)
  DirMode = 2
  FaceMakerClass = Part::FaceMakerBullseye
  LengthFwd = -6.5
  LengthRev = 0
  Placement = pos=(0,-15.45,20.3) rot=(1,0,0;1.5708rad)
  Solid = true
  Symmetric = false
FEATURE [Part::Fillet] Fillet013  label="solenoidDriverBottomLipTopFillet006"
  Base = -> Extrude022
  Edges = 1 edges r=1.4: [Edge6]
  Placement = pos=(5,0,0) rot=(0,0,1;0rad)
FEATURE [Sketcher::SketchObject] Sketch026
  FullyConstrained = true
  Placement = pos=(0,-14.3,2.37) rot=(-1,0,0;2.03453rad)
  sketch-geometry (4):
    g0: LineSegment StartX=0 StartY=1.5 StartZ=0 EndX=0 EndY=0 EndZ=0
    g1: LineSegment StartX=0 StartY=1.5 StartZ=0 EndX=5 EndY=1.5 EndZ=0
    g2: LineSegment StartX=5 StartY=1.5 StartZ=0 EndX=5 EndY=0 EndZ=0
    g3: LineSegment StartX=0 StartY=0 StartZ=0 EndX=5 EndY=0 EndZ=0
  constraints (13):
    c: Vertical(g0)
    c: Distance(g0) = 1.5
    c: Horizontal(g1)
    c: Distance(g1) = 5
    c: Coincident(g1,g0)
    c: Vertical(g2)
    c: Distance(g2) = 1.5
    c: Coincident(g2,g1)
    c: Block(g1)
    c: Block(g2)
    c: Block(g0)
    c: Coincident(g3,g0)
    c: Coincident(g3,g2)
FEATURE [Part::Extrusion] Extrude023  label="solenoidDriverBottomLipTopExtrude015"
  Base = -> Sketch026
  Dir = (0,0.894389,-0.447291)
  DirMode = 2
  FaceMakerClass = Part::FaceMakerBullseye
  LengthFwd = -6.5
  LengthRev = 0
  Placement = pos=(5,-14.15,19.65) rot=(1,0,0;1.5708rad)
  Solid = true
  Symmetric = false
FEATURE [Sketcher::SketchObject] Sketch027
  FullyConstrained = true
  Placement = pos=(0,-14.3,2.37) rot=(-1,0,0;2.03453rad)
  sketch-geometry (5):
    g0: LineSegment StartX=45.5 StartY=-21.2 StartZ=0 EndX=49.5 EndY=-21.2 EndZ=0
    g1: LineSegment StartX=49.5 StartY=0 StartZ=0 EndX=49.5 EndY=-21.2 EndZ=0
    g2: LineSegment StartX=49.5 StartY=0 StartZ=0 EndX=49.5 EndY=1.6 EndZ=0
    g3: LineSegment StartX=45.5 StartY=-21.2 StartZ=0 EndX=45.5 EndY=1.6 EndZ=0
    g4: LineSegment StartX=49.5 StartY=1.6 StartZ=0 EndX=45.5 EndY=1.6 EndZ=0
  constraints (14):
    c: Horizontal(g0)
    c: Distance(g0) = 4
    c: Coincident(g1,g0)
    c: Vertical(g1)
    c: Block(g1)
    c: Vertical(g2)
    c: Distance(g2) = 1.6
    c: Block(g2)
    c: Coincident(g3,g0)
    c: Vertical(g3)
    c: Coincident(g4,g2)
    c: Horizontal(g4)
    c: Block(g0)
    c: Coincident(g3,g4)
FEATURE [Part::Extrusion] Extrude024
  Base = -> Sketch027
  Dir = (0,0.894389,-0.447291)
  DirMode = 2
  FaceMakerClass = Part::FaceMakerBullseye
  LengthFwd = 6.34
  LengthRev = 0
  Placement = pos=(0,-5.59,1) rot=(0,0,1;0rad)
  Solid = true
  Symmetric = false
FEATURE [Part::Fillet] Fillet014  label="solenoidDriverSideBarFillet014"
  Base = -> Extrude024
  Edges = 1 edges r=1.4: [Edge14]
  Placement = pos=(0,0.9,-0.45) rot=(0,0,1;0rad)
FEATURE [Part::Revolution] Revolve  label="mainScrewStandRevolve"
  Angle = 360
  Axis = (0,0,1)
  Base = (0,0,0)
  FaceMakerClass = Part::FaceMakerBullseye
  Placement = pos=(121.35,-15.3,0) rot=(0,0,1;0rad)
  Solid = true
  Source = -> Sketch004
  Symmetric = false
FEATURE [Part::Extrusion] Extrude021  label="solenoidDriverTopLipLowerExtrude011"
  Base = -> Sketch024
  Dir = (0,0.894389,-0.447291)
  DirMode = 2
  FaceMakerClass = Part::FaceMakerBullseye
  LengthFwd = 5.05
  LengthRev = 0
  Solid = true
  Symmetric = false
FEATURE [Part::Fillet] Fillet012  label="solenoidDriverTopLipLowerFillet004"
  Base = -> Extrude021
  Edges = 1 edges r=1.2: [Edge7]
  Placement = pos=(0,-0.9,-1.35) rot=(0,0,1;0rad)
FEATURE [Part::Fillet] Fillet003  label="solenoidDriverTopLipLowerFillet003"
  Base = -> Extrude010
  Edges = 1 edges r=1.2: [Edge7]
  Placement = pos=(0,-3,-0.3) rot=(0,0,1;0rad)
FEATURE [Part::Extrusion] Extrude025  label="mainBodyUpperExtrude025"
  Base = -> Sketch001
  Dir = (0,0,1)
  DirMode = 2
  FaceMakerClass = Part::FaceMakerBullseye
  LengthFwd = 20
  LengthRev = 0
  Solid = true
  Symmetric = false
FEATURE [Part::MultiFuse] Fusion  label="solenoidDriverBottomLipFusion"
  Placement = pos=(0,-1.6,0) rot=(0,0,1;0rad)
  Shapes = -> [Fillet005,Fillet013,Extrude023,Extrude013]
FEATURE [Sketcher::SketchObject] Sketch028
  FullyConstrained = true
  Placement = pos=(0,-14.3,2.37) rot=(-1,0,0;2.03453rad)
  sketch-geometry (4):
    g0: LineSegment StartX=0 StartY=1.5 StartZ=0 EndX=0 EndY=0 EndZ=0
    g1: LineSegment StartX=0 StartY=1.5 StartZ=0 EndX=5 EndY=1.5 EndZ=0
    g2: LineSegment StartX=5 StartY=1.5 StartZ=0 EndX=5 EndY=0 EndZ=0
    g3: LineSegment StartX=0 StartY=0 StartZ=0 EndX=5 EndY=0 EndZ=0
  constraints (13):
    c: Vertical(g0)
    c: Distance(g0) = 1.5
    c: Horizontal(g1)
    c: Distance(g1) = 5
    c: Coincident(g1,g0)
    c: Vertical(g2)
    c: Distance(g2) = 1.5
    c: Coincident(g2,g1)
    c: Block(g1)
    c: Block(g2)
    c: Block(g0)
    c: Coincident(g3,g0)
    c: Coincident(g3,g2)
FEATURE [Part::Extrusion] Extrude026  label="solenoidDriverBottomLipTopExtrude016"
  Base = -> Sketch028
  Dir = (0,0.894389,-0.447291)
  DirMode = 2
  FaceMakerClass = Part::FaceMakerBullseye
  LengthFwd = -6.5
  LengthRev = 0
  Placement = pos=(5,-14.15,19.65) rot=(1,0,0;1.5708rad)
  Solid = true
  Symmetric = false
FEATURE [Sketcher::SketchObject] Sketch029
  FullyConstrained = true
  Placement = pos=(0,-14.3,2.37) rot=(-1,0,0;2.03453rad)
  sketch-geometry (4):
    g0: LineSegment StartX=0 StartY=1.5 StartZ=0 EndX=0 EndY=0 EndZ=0
    g1: LineSegment StartX=0 StartY=1.5 StartZ=0 EndX=5 EndY=1.5 EndZ=0
    g2: LineSegment StartX=5 StartY=1.5 StartZ=0 EndX=5 EndY=0 EndZ=0
    g3: LineSegment StartX=0 StartY=0 StartZ=0 EndX=5 EndY=0 EndZ=0
  constraints (13):
    c: Vertical(g0)
    c: Distance(g0) = 1.5
    c: Horizontal(g1)
    c: Distance(g1) = 5
    c: Coincident(g1,g0)
    c: Vertical(g2)
    c: Distance(g2) = 1.5
    c: Coincident(g2,g1)
    c: Block(g1)
    c: Block(g2)
    c: Block(g0)
    c: Coincident(g3,g0)
    c: Coincident(g3,g2)
FEATURE [Part::Extrusion] Extrude027  label="solenoidDriverBottomLipTopExtrude017"
  Base = -> Sketch029
  Dir = (0,0.894389,-0.447291)
  DirMode = 2
  FaceMakerClass = Part::FaceMakerBullseye
  LengthFwd = -6.5
  LengthRev = 0
  Placement = pos=(0,-14.15,19.65) rot=(1,0,0;1.5708rad)
  Solid = true
  Symmetric = false
FEATURE [Sketcher::SketchObject] Sketch030
  FullyConstrained = true
  Placement = pos=(0,-14.3,2.37) rot=(-1,0,0;2.03453rad)
  sketch-geometry (4):
    g0: LineSegment StartX=0 StartY=1.5 StartZ=0 EndX=0 EndY=0 EndZ=0
    g1: LineSegment StartX=0 StartY=1.5 StartZ=0 EndX=5 EndY=1.5 EndZ=0
    g2: LineSegment StartX=5 StartY=1.5 StartZ=0 EndX=5 EndY=0 EndZ=0
    g3: LineSegment StartX=0 StartY=0 StartZ=0 EndX=5 EndY=0 EndZ=0
  constraints (13):
    c: Vertical(g0)
    c: Distance(g0) = 1.5
    c: Horizontal(g1)
    c: Distance(g1) = 5
    c: Coincident(g1,g0)
    c: Vertical(g2)
    c: Distance(g2) = 1.5
    c: Coincident(g2,g1)
    c: Block(g1)
    c: Block(g2)
    c: Block(g0)
    c: Coincident(g3,g0)
    c: Coincident(g3,g2)
FEATURE [Sketcher::SketchObject] Sketch031
  FullyConstrained = true
  Placement = pos=(0,-14.3,2.37) rot=(-1,0,0;2.03453rad)
  sketch-geometry (6):
    g0: LineSegment StartX=45.5 StartY=-21.2 StartZ=0 EndX=49.5 EndY=-21.2 EndZ=0
    g1: LineSegment StartX=45.5 StartY=0 StartZ=0 EndX=49.5 EndY=0 EndZ=0
    g2: LineSegment StartX=49.5 StartY=0 StartZ=0 EndX=49.5 EndY=-21.2 EndZ=0
    g3: LineSegment StartX=4 StartY=0 StartZ=0 EndX=4 EndY=-21.2 EndZ=0
    g4: LineSegment StartX=45.5 StartY=-21.2 StartZ=0 EndX=4 EndY=-21.2 EndZ=0
    g5: LineSegment StartX=4 StartY=0 StartZ=0 EndX=45.5 EndY=0 EndZ=0
  constraints (16):
    c: Horizontal(g0)
    c: Distance(g0) = 4
    c: Horizontal(g1)
    c: Distance(g1) = 4
    c: Coincident(g2,g1)
    c: Coincident(g2,g0)
    c: Vertical(g2)
    c: Block(g2)
    c: Vertical(g3)
    c: Coincident(g4,g0)
    c: Horizontal(g4)
    c: Coincident(g4,g3)
    c: Coincident(g5,g1)
    c: Horizontal(g5)
    c: Block(g3)
    c: Block(g5)
FEATURE [Part::Extrusion] Extrude028  label="removeFromSolenoidDriverMainExtrude021"
  Base = -> Sketch031
  Dir = (0,0.894389,-0.447291)
  DirMode = 2
  FaceMakerClass = Part::FaceMakerBullseye
  LengthFwd = 3.1
  LengthRev = 0
  Placement = pos=(-4,-2.42,-0.8) rot=(0,0,1;0rad)
  Solid = true
  Symmetric = false
FEATURE [Part::Extrusion] Extrude029  label="solenoidDriverBottomLipTopExtrude018"
  Base = -> Sketch030
  Dir = (0,0.894389,-0.447291)
  DirMode = 2
  FaceMakerClass = Part::FaceMakerBullseye
  LengthFwd = -6.5
  LengthRev = 0
  Placement = pos=(5,-14.15,19.65) rot=(1,0,0;1.5708rad)
  Solid = true
  Symmetric = false
FEATURE [Sketcher::SketchObject] Sketch032
  FullyConstrained = true
  Placement = pos=(0,-14.3,2.37) rot=(-1,0,0;2.03453rad)
  sketch-geometry (4):
    g0: LineSegment StartX=0 StartY=1.5 StartZ=0 EndX=0 EndY=0 EndZ=0
    g1: LineSegment StartX=0 StartY=1.5 StartZ=0 EndX=5 EndY=1.5 EndZ=0
    g2: LineSegment StartX=5 StartY=1.5 StartZ=0 EndX=5 EndY=0 EndZ=0
    g3: LineSegment StartX=0 StartY=0 StartZ=0 EndX=5 EndY=0 EndZ=0
  constraints (13):
    c: Vertical(g0)
    c: Distance(g0) = 1.5
    c: Horizontal(g1)
    c: Distance(g1) = 5
    c: Coincident(g1,g0)
    c: Vertical(g2)
    c: Distance(g2) = 1.5
    c: Coincident(g2,g1)
    c: Block(g1)
    c: Block(g2)
    c: Block(g0)
    c: Coincident(g3,g0)
    c: Coincident(g3,g2)
FEATURE [Part::Extrusion] Extrude030  label="solenoidDriverBottomLipTopExtrude019"
  Base = -> Sketch032
  Dir = (0,0.894389,-0.447291)
  DirMode = 2
  FaceMakerClass = Part::FaceMakerBullseye
  LengthFwd = -6.5
  LengthRev = 0
  Placement = pos=(0,-14.15,19.65) rot=(1,0,0;1.5708rad)
  Solid = true
  Symmetric = false
FEATURE [Part::MultiFuse] Fusion004
  Placement = pos=(0,1.4,2.65) rot=(0,0,1;0rad)
  Shapes = -> [Extrude029,Extrude030]
FEATURE [Part::MultiFuse] Fusion003
  Placement = pos=(-2.3,0,0) rot=(0,0,1;0rad)
  Shapes = -> [Extrude028,Fusion004]
FEATURE [Sketcher::SketchObject] Sketch033
  FullyConstrained = true
  Placement = pos=(0,-14.3,2.37) rot=(-1,0,0;2.03453rad)
  sketch-geometry (4):
    g0: LineSegment StartX=0 StartY=1.5 StartZ=0 EndX=0 EndY=0 EndZ=0
    g1: LineSegment StartX=0 StartY=1.5 StartZ=0 EndX=5 EndY=1.5 EndZ=0
    g2: LineSegment StartX=5 StartY=1.5 StartZ=0 EndX=5 EndY=0 EndZ=0
    g3: LineSegment StartX=0 StartY=0 StartZ=0 EndX=5 EndY=0 EndZ=0
  constraints (13):
    c: Vertical(g0)
    c: Distance(g0) = 1.5
    c: Horizontal(g1)
    c: Distance(g1) = 5
    c: Coincident(g1,g0)
    c: Vertical(g2)
    c: Distance(g2) = 1.5
    c: Coincident(g2,g1)
    c: Block(g1)
    c: Block(g2)
    c: Block(g0)
    c: Coincident(g3,g0)
    c: Coincident(g3,g2)
FEATURE [Sketcher::SketchObject] Sketch034
  FullyConstrained = true
  Placement = pos=(0,-14.3,2.37) rot=(-1,0,0;2.03453rad)
  sketch-geometry (4):
    g0: LineSegment StartX=0 StartY=1.5 StartZ=0 EndX=4 EndY=1.5 EndZ=0
    g1: LineSegment StartX=4 StartY=1.5 StartZ=0 EndX=4 EndY=-2.5 EndZ=0
    g2: LineSegment StartX=4 StartY=-2.5 StartZ=0 EndX=0 EndY=-2.5 EndZ=0
    g3: LineSegment StartX=0 StartY=1.5 StartZ=0 EndX=0 EndY=-2.5 EndZ=0
  constraints (11):
    c: Horizontal(g0)
    c: Distance(g0) = 4
    c: Block(g0)
    c: Coincident(g1,g0)
    c: Vertical(g1)
    c: Distance(g1) = 4
    c: Coincident(g2,g1)
    c: Horizontal(g2)
    c: Distance(g2) = 4
    c: Coincident(g3,g0)
    c: Coincident(g3,g2)
FEATURE [Part::Extrusion] Extrude020  label="removeFromSolenoidDriverMainExtrude020"
  Base = -> Sketch020
  Dir = (0,0.894389,-0.447291)
  DirMode = 2
  FaceMakerClass = Part::FaceMakerBullseye
  LengthFwd = 3.1
  LengthRev = 0
  Placement = pos=(-4,-2.42,-0.8) rot=(0,0,1;0rad)
  Solid = true
  Symmetric = false
FEATURE [Part::Fillet] Fillet
  Base = -> Fusion003
  Edges = 1 edges r=10: [Edge5]
  Placement = pos=(-2,0,0) rot=(0,0,1;0rad)
FEATURE [Part::MultiFuse] Fusion001
  Placement = pos=(0,1.4,2.65) rot=(0,0,1;0rad)
  Shapes = -> [Extrude026,Extrude027]
FEATURE [Part::MultiFuse] Fusion002
  Shapes = -> [Extrude020,Fusion001]
FEATURE [Sketcher::SketchObject] Sketch035
  FullyConstrained = true
  Placement = pos=(0,-14.3,2.37) rot=(-1,0,0;2.03453rad)
  sketch-geometry (4):
    g0: LineSegment StartX=0 StartY=1.5 StartZ=0 EndX=0 EndY=0 EndZ=0
    g1: LineSegment StartX=0 StartY=1.5 StartZ=0 EndX=5 EndY=1.5 EndZ=0
    g2: LineSegment StartX=5 StartY=1.5 StartZ=0 EndX=5 EndY=0 EndZ=0
    g3: LineSegment StartX=0 StartY=0 StartZ=0 EndX=5 EndY=0 EndZ=0
  constraints (13):
    c: Vertical(g0)
    c: Distance(g0) = 1.5
    c: Horizontal(g1)
    c: Distance(g1) = 5
    c: Coincident(g1,g0)
    c: Vertical(g2)
    c: Distance(g2) = 1.5
    c: Coincident(g2,g1)
    c: Block(g1)
    c: Block(g2)
    c: Block(g0)
    c: Coincident(g3,g0)
    c: Coincident(g3,g2)
FEATURE [Sketcher::SketchObject] Sketch036
  FullyConstrained = true
  Placement = pos=(0,-14.3,2.37) rot=(-1,0,0;2.03453rad)
  sketch-geometry (4):
    g0: LineSegment StartX=0 StartY=1.5 StartZ=0 EndX=0 EndY=0 EndZ=0
    g1: LineSegment StartX=0 StartY=1.5 StartZ=0 EndX=5 EndY=1.5 EndZ=0
    g2: LineSegment StartX=5 StartY=1.5 StartZ=0 EndX=5 EndY=0 EndZ=0
    g3: LineSegment StartX=0 StartY=0 StartZ=0 EndX=5 EndY=0 EndZ=0
  constraints (13):
    c: Vertical(g0)
    c: Distance(g0) = 1.5
    c: Horizontal(g1)
    c: Distance(g1) = 5
    c: Coincident(g1,g0)
    c: Vertical(g2)
    c: Distance(g2) = 1.5
    c: Coincident(g2,g1)
    c: Block(g1)
    c: Block(g2)
    c: Block(g0)
    c: Coincident(g3,g0)
    c: Coincident(g3,g2)
FEATURE [Part::Extrusion] Extrude031  label="solenoidDriverBottomLipTopExtrude020"
  Base = -> Sketch035
  Dir = (0,0.894389,-0.447291)
  DirMode = 2
  FaceMakerClass = Part::FaceMakerBullseye
  LengthFwd = -6.5
  LengthRev = 0
  Placement = pos=(5,-14.15,19.65) rot=(1,0,0;1.5708rad)
  Solid = true
  Symmetric = false
FEATURE [Part::Extrusion] Extrude032  label="solenoidDriverBottomLipTopExtrude021"
  Base = -> Sketch036
  Dir = (0,0.894389,-0.447291)
  DirMode = 2
  FaceMakerClass = Part::FaceMakerBullseye
  LengthFwd = -6.5
  LengthRev = 0
  Placement = pos=(0,-14.15,19.65) rot=(1,0,0;1.5708rad)
  Solid = true
  Symmetric = false
FEATURE [Part::MultiFuse] Fusion009
  Placement = pos=(8,1.4,2.65) rot=(0,0,1;0rad)
  Shapes = -> [Extrude031,Extrude032]
FEATURE [Part::MultiFuse] Fusion010  label="removeFromSolenoidDriver"
  Shapes = -> [Fusion009,Fillet,Fusion002]
FEATURE [Sketcher::SketchObject] Sketch037
  FullyConstrained = true
  Placement = pos=(0,0,0) rot=(1,0,0;1.5708rad)
  sketch-geometry (4):
    g0: Circle CenterX=64.05 CenterY=16.5 CenterZ=0 NormalX=0 NormalY=0 NormalZ=1 AngleXU=0 Radius=2.7
    g1: Circle CenterX=64.05 CenterY=8.5 CenterZ=0 NormalX=0 NormalY=0 NormalZ=1 AngleXU=0 Radius=2.7
    g2: Circle CenterX=84.15 CenterY=8.5 CenterZ=0 NormalX=0 NormalY=0 NormalZ=1 AngleXU=0 Radius=2.7
    g3: Circle CenterX=84.15 CenterY=16.5 CenterZ=0 NormalX=0 NormalY=0 NormalZ=1 AngleXU=0 Radius=2.7
  constraints (4):
    c: Block(g2)
    c: Block(g3)
    c: Block(g0)
    c: Block(g1)
FEATURE [Part::Extrusion] Extrude033  label="removeFromMainBodyToCreateScrewHoleCounterSinks001"
  Base = -> Sketch037
  Dir = (0,-1,1.1e-15)
  DirMode = 2
  FaceMakerClass = Part::FaceMakerBullseye
  LengthFwd = 1.9
  LengthRev = 0
  Placement = pos=(0.8,0,0) rot=(0,0,1;0rad)
  Solid = true
  Symmetric = false
FEATURE [Part::MultiFuse] Fusion011  label="removeFromMainBodyToCreateScrewHoleCounterSinks001Fusion011"
  Shapes = -> [Extrude014,Extrude033]
FEATURE [Sketcher::SketchObject] Sketch038
  FullyConstrained = true
  Placement = pos=(0,-14.3,2.37) rot=(-1,0,0;2.03453rad)
  sketch-geometry (4):
    g0: LineSegment StartX=33.9 StartY=-9.7 StartZ=0 EndX=33.9 EndY=-1.5 EndZ=0
    g1: LineSegment StartX=33.9 StartY=-1.5 StartZ=0 EndX=44.5 EndY=-1.5 EndZ=0
    g2: LineSegment StartX=33.9 StartY=-9.7 StartZ=0 EndX=44.5 EndY=-9.7 EndZ=0
    g3: LineSegment StartX=44.5 StartY=-1.5 StartZ=0 EndX=44.5 EndY=-9.7 EndZ=0
  constraints (10):
    c: Vertical(g0)
    c: Coincident(g1,g0)
    c: Horizontal(g1)
    c: Block(g1)
    c: Block(g0)
    c: Coincident(g2,g0)
    c: Horizontal(g2)
    c: Coincident(g3,g1)
    c: Coincident(g3,g2)
    c: Vertical(g3)
FEATURE [Part::Extrusion] Extrude034
  Base = -> Sketch038
  Dir = (0,0.894389,-0.447291)
  DirMode = 2
  FaceMakerClass = Part::FaceMakerBullseye
  LengthFwd = 16
  LengthRev = 0
  Placement = pos=(0,-22,7) rot=(0,0,1;0rad)
  Solid = true
  Symmetric = false
FEATURE [Sketcher::SketchObject] Sketch039
  FullyConstrained = true
  Placement = pos=(0,-14.3,2.37) rot=(-1,0,0;2.03453rad)
  sketch-geometry (4):
    g0: LineSegment StartX=5.5 StartY=-7.7 StartZ=0 EndX=13.3 EndY=-7.7 EndZ=0
    g1: LineSegment StartX=13.3 StartY=-7.7 StartZ=0 EndX=13.3 EndY=-13.1 EndZ=0
    g2: LineSegment StartX=13.3 StartY=-13.1 StartZ=0 EndX=5.5 EndY=-13.1 EndZ=0
    g3: LineSegment StartX=5.5 StartY=-7.7 StartZ=0 EndX=5.5 EndY=-13.1 EndZ=0
  constraints (12):
    c: Horizontal(g0)
    c: Distance(g0) = 7.8
    c: Coincident(g1,g0)
    c: Vertical(g1)
    c: Distance(g1) = 5.4
    c: Coincident(g2,g1)
    c: Horizontal(g2)
    c: Vertical(g3)
    c: Coincident(g3,g2)
    c: Block(g0)
    c: Block(g2)
    c: Block(g3)
FEATURE [Part::Extrusion] Extrude035  label="removeToMakeHoleForConnectorExtrude035"
  Base = -> Sketch039
  Dir = (0,0.894389,-0.447291)
  DirMode = 2
  FaceMakerClass = Part::FaceMakerBullseye
  LengthFwd = 15
  LengthRev = 0
  Placement = pos=(-4,-22,9.6469) rot=(0,0,1;0rad)
  Solid = true
  Symmetric = false
FEATURE [App::MeasureDistance] Distance  label="Distance: 4.00 mm"
  Distance = 4.00184
  P1 = (119.349,-15.3,8)
  P2 = (123.351,-15.3,8)
FEATURE [App::MeasureDistance] Distance001  label="Distance: 3.80 mm"
  Distance = 3.8
  P1 = (119.45,-15.3,8)
  P2 = (123.25,-15.3,8)
FEATURE [Part::Fillet] Fillet015
  Base = -> Extrude009
  Edges = 1 edges r=1.59: [Edge7]
FEATURE [Part::Fillet] Fillet016
  Base = -> Extrude017
  Edges = 1 edges r=1.49: [Edge12]
FEATURE [Part::Fillet] Fillet017
  Base = -> Fillet016
  Edges = 1 edges r=1.45: [Edge8]
FEATURE [Part::MultiFuse] Fusion012  label="main"
  Shapes = -> [Extrude,Revolve,Extrude005,Fillet003,Fillet012,Fillet014,Extrude025,Fusion,Fillet015,Fillet017]
FEATURE [Part::Cut] Cut001
  Base = -> Fusion012
  Tool = -> Box003
FEATURE [Part::Cut] Cut002
  Base = -> Cut001
  Tool = -> Box002
FEATURE [Part::Cut] Cut003
  Base = -> Cut002
  Tool = -> Cut
FEATURE [Part::Cut] Cut004
  Base = -> Cut003
  Tool = -> Extrude019
FEATURE [Part::Cut] Cut005
  Base = -> Cut004
  Tool = -> Fusion011
FEATURE [Part::Cut] Cut006
  Base = -> Cut005
  Tool = -> Extrude004
FEATURE [Part::Cut] Cut007
  Base = -> Cut006
  Tool = -> Extrude015
FEATURE [Part::Cut] Cut008
  Base = -> Cut007
  Tool = -> Extrude008
FEATURE [Part::Cut] Cut009
  Base = -> Cut008
  Tool = -> Fusion010
FEATURE [App::MeasureDistance] Distance002  label="Distance: 2.05 mm"
  Distance = 2.05453
  P1 = (1.5,-23.0732,21.402)
  P2 = (6e-15,-23,20)
FEATURE [Part::Cut] Cut010
  Base = -> Cut009
  Tool = -> Extrude035
FEATURE [Part::Cut] Cut011
  Base = -> Cut010
  Tool = -> Extrude034
FEATURE [Part::Box] Box004  label="Cube004"
  AttacherType = Attacher::AttachEngine3D
  Height = 10
  Length = 200
  Placement = pos=(-30,0,0) rot=(0,0,1;0rad)
  Width = 10
FEATURE [Part::Fillet] Fillet020
  Base = -> Box004
  Edges = 1 edges r=3.6: [Edge12]
FEATURE [Part::Box] Box005  label="Cube005"
  AttacherType = Attacher::AttachEngine3D
  Height = 10
  Length = 198
  Placement = pos=(-30,0,0) rot=(0,0,1;0rad)
  Width = 10
FEATURE [Part::Cut] Cut012
  Base = -> Box005
  Tool = -> Fillet020
FEATURE [Part::Box] Box006  label="Cube006"
  AttacherType = Attacher::AttachEngine3D
  Height = 5
  Length = 200
  Placement = pos=(-30,6.4,10) rot=(1,0,0;0rad)
  Width = 5
FEATURE [Part::Box] Box007  label="Cube007"
  AttacherType = Attacher::AttachEngine3D
  Height = 5
  Length = 200
  Placement = pos=(-30,6.4,10) rot=(1,0,0;0.872665rad)
  Width = 5
FEATURE [Part::MultiFuse] Fusion013  label="removeFromMainFusion013"
  Placement = pos=(0,-10,10) rot=(0,0,1;0rad)
  Shapes = -> [Box007,Box006,Cut012]
FEATURE [Mesh::Feature] v0_98_Cut013  label="v0_98-Cut013"
FEATURE [App::MeasureDistance] Distance003  label="Distance: 7.18 mm"
  Distance = 7.17719
  P1 = (117.773,-15.3145,-2.4)
  P2 = (124.951,-15.2973,-2.4)
FEATURE [Sketcher::SketchObject] Sketch040
  FullyConstrained = true
  Placement = pos=(0,-14.3,2.37) rot=(-1,0,0;2.03453rad)
  sketch-geometry (4):
    g0: LineSegment StartX=0 StartY=1.5 StartZ=0 EndX=0 EndY=0 EndZ=0
    g1: LineSegment StartX=0 StartY=1.5 StartZ=0 EndX=5 EndY=1.5 EndZ=0
    g2: LineSegment StartX=5 StartY=1.5 StartZ=0 EndX=5 EndY=0 EndZ=0
    g3: LineSegment StartX=0 StartY=0 StartZ=0 EndX=5 EndY=0 EndZ=0
  constraints (13):
    c: Vertical(g0)
    c: Distance(g0) = 1.5
    c: Horizontal(g1)
    c: Distance(g1) = 5
    c: Coincident(g1,g0)
    c: Vertical(g2)
    c: Distance(g2) = 1.5
    c: Coincident(g2,g1)
    c: Block(g1)
    c: Block(g2)
    c: Block(g0)
    c: Coincident(g3,g0)
    c: Coincident(g3,g2)
FEATURE [Part::Extrusion] Extrude036
  Base = -> Sketch040
  Dir = (0,0.894389,-0.447291)
  DirMode = 2
  FaceMakerClass = Part::FaceMakerBullseye
  LengthFwd = 1.4
  LengthRev = 0
  Placement = pos=(0,8.25,17.58) rot=(0,0,1;0rad)
  Solid = true
  Symmetric = false
FEATURE [Sketcher::SketchObject] Sketch041
  FullyConstrained = true
  Placement = pos=(0,-14.3,2.37) rot=(-1,0,0;2.03453rad)
  sketch-geometry (4):
    g0: LineSegment StartX=0 StartY=1.5 StartZ=0 EndX=0 EndY=0 EndZ=0
    g1: LineSegment StartX=0 StartY=1.5 StartZ=0 EndX=5 EndY=1.5 EndZ=0
    g2: LineSegment StartX=5 StartY=1.5 StartZ=0 EndX=5 EndY=0 EndZ=0
    g3: LineSegment StartX=0 StartY=0 StartZ=0 EndX=5 EndY=0 EndZ=0
  constraints (13):
    c: Vertical(g0)
    c: Distance(g0) = 1.5
    c: Horizontal(g1)
    c: Distance(g1) = 5
    c: Coincident(g1,g0)
    c: Vertical(g2)
    c: Distance(g2) = 1.5
    c: Coincident(g2,g1)
    c: Block(g1)
    c: Block(g2)
    c: Block(g0)
    c: Coincident(g3,g0)
    c: Coincident(g3,g2)
FEATURE [Part::Extrusion] Extrude037
  Base = -> Sketch041
  Dir = (0,0.894389,-0.447291)
  DirMode = 2
  FaceMakerClass = Part::FaceMakerBullseye
  LengthFwd = 1.4
  LengthRev = 0
  Placement = pos=(0,6.11,13.33) rot=(0,0,1;0rad)
  Solid = true
  Symmetric = false
FEATURE [Part::MultiFuse] Fusion014  label="screwSpacerFusion014"
  Shapes = -> [Extrude037,Extrude036]
FEATURE [Sketcher::SketchObject] Sketch042
  FullyConstrained = true
  Placement = pos=(0,-14.3,2.37) rot=(-1,0,0;2.03453rad)
  sketch-geometry (4):
    g0: LineSegment StartX=0 StartY=1.5 StartZ=0 EndX=0 EndY=0 EndZ=0
    g1: LineSegment StartX=0 StartY=1.5 StartZ=0 EndX=5 EndY=1.5 EndZ=0
    g2: LineSegment StartX=5 StartY=1.5 StartZ=0 EndX=5 EndY=0 EndZ=0
    g3: LineSegment StartX=0 StartY=0 StartZ=0 EndX=5 EndY=0 EndZ=0
  constraints (13):
    c: Vertical(g0)
    c: Distance(g0) = 1.5
    c: Horizontal(g1)
    c: Distance(g1) = 5
    c: Coincident(g1,g0)
    c: Vertical(g2)
    c: Distance(g2) = 1.5
    c: Coincident(g2,g1)
    c: Block(g1)
    c: Block(g2)
    c: Block(g0)
    c: Coincident(g3,g0)
    c: Coincident(g3,g2)
FEATURE [Part::Extrusion] Extrude038
  Base = -> Sketch042
  Dir = (0,0.894389,-0.447291)
  DirMode = 2
  FaceMakerClass = Part::FaceMakerBullseye
  LengthFwd = 1.4
  LengthRev = 0
  Placement = pos=(0,8.459,18) rot=(0,0,1;0rad)
  Solid = true
  Symmetric = false
FEATURE [Part::MultiFuse] Fusion015  label="screwSpacerFusion014Fusion015"
  Placement = pos=(0,0.35,-0.18) rot=(0,0,1;0rad)
  Shapes = -> [Extrude038,Fusion014]
FEATURE [Part::Cylinder] Cylinder
  Angle = 360
  AttacherType = Attacher::AttachEngine3D
  Height = 10
  Placement = pos=(0,10,0) rot=(0,0,1;0rad)
  Radius = 1.5
FEATURE [Part::Cylinder] Cylinder001
  Angle = 360
  AttacherType = Attacher::AttachEngine3D
  Height = 10
  Placement = pos=(3,10,0) rot=(0,0,1;0rad)
  Radius = 1.5
FEATURE [Part::Box] Box008  label="Cube008"
  AttacherType = Attacher::AttachEngine3D
  Height = 10
  Length = 3
  Placement = pos=(0,8.5,0) rot=(0,0,1;0rad)
  Width = 3
FEATURE [Part::MultiFuse] Fusion016  label="holeForWireFusion016"
  Shapes = -> [Cylinder001,Box008,Cylinder]
FEATURE [Part::Box] Box009  label="Cube009"
  AttacherType = Attacher::AttachEngine3D
  Height = 10
  Length = 3
  Placement = pos=(0,8.5,0) rot=(0,0,1;0rad)
  Width = 3
FEATURE [Part::Cylinder] Cylinder002
  Angle = 360
  AttacherType = Attacher::AttachEngine3D
  Height = 10
  Placement = pos=(0,10,0) rot=(0,0,1;0rad)
  Radius = 1.5
FEATURE [Part::Cylinder] Cylinder003
  Angle = 360
  AttacherType = Attacher::AttachEngine3D
  Height = 10
  Placement = pos=(3,10,0) rot=(0,0,1;0rad)
  Radius = 1.5
FEATURE [Part::MultiFuse] Fusion017  label="holeForWireFusion017"
  Placement = pos=(0,0,10) rot=(0,0,1;0rad)
  Shapes = -> [Cylinder003,Box009,Cylinder002]
FEATURE [Part::MultiFuse] Fusion018  label="holeForWireFusion018"
  Placement = pos=(0,0,0) rot=(0,1,0;-1.5708rad)
  Shapes = -> [Fusion017,Fusion016]
FEATURE [Part::Box] Box010  label="Cube010"
  AttacherType = Attacher::AttachEngine3D
  Height = 0.1
  Length = 0.1
  Placement = pos=(-2,10,0) rot=(0,0.995037,0.099504;0rad)
  Width = 0.1
FEATURE [Part::MultiFuse] Fusion019
  Placement = pos=(0,10,0) rot=(1,0,0;1.5708rad)
  Shapes = -> [Box010,Fusion018]
FEATURE [Part::Box] Box011  label="Cube011"
  AttacherType = Attacher::AttachEngine3D
  Height = 0.1
  Length = 1.1
  Placement = pos=(-2,10,10) rot=(0,0.995037,0.099504;0rad)
  Width = 0.1
FEATURE [Part::MultiFuse] Fusion020
  Placement = pos=(0,0,0) rot=(0,1,0;0.349066rad)
  Shapes = -> [Box011,Fusion019]
FEATURE [Part::Box] Box012  label="Cube012"
  AttacherType = Attacher::AttachEngine3D
  Height = 0.1
  Length = 1.1
  Placement = pos=(-2,10,10) rot=(0,0.995037,0.099504;0rad)
  Width = 0.1
FEATURE [Part::MultiFuse] Fusion021
  Placement = pos=(0,30,0) rot=(0,0,1;-2.6529rad)
  Shapes = -> [Box012,Fusion020]
FEATURE [Part::Box] Box013  label="Cube013"
  AttacherType = Attacher::AttachEngine3D
  Height = 0.1
  Length = 1.1
  Placement = pos=(2,19,10) rot=(0,0.995037,0.099504;0rad)
  Width = 0.1
FEATURE [Part::MultiFuse] Fusion022  label="holeForWire"
  Placement = pos=(15,-49.8,-8.2) rot=(0,0,1;0rad)
  Shapes = -> [Box013,Fusion021]
FEATURE [Part::Cut] Cut013
  Base = -> Cut011
  Tool = -> Fusion013
FEATURE [Part::Cut] Cut014
  Base = -> Cut013
  Tool = -> Fusion022
FEATURE [Sketcher::SketchObject] Sketch043
  FullyConstrained = true
  MapMode = 4
  Placement = pos=(0,0,0) rot=(0.57735,0.57735,0.57735;2.0944rad)
  Support = -> [Cut014]
  sketch-geometry (14):
    g0: LineSegment StartX=6.08745 StartY=-4.11588 StartZ=0 EndX=6.08745 EndY=-2.11589 EndZ=0
    g1: LineSegment StartX=3.58745 StartY=2.38411 StartZ=0 EndX=3.58745 EndY=4.38411 EndZ=0
    g2: LineSegment StartX=8.08745 StartY=1.38411 StartZ=0 EndX=8.08745 EndY=-1.11589 EndZ=0
    g3: ArcOfCircle CenterX=7.08745 CenterY=-1.11589 CenterZ=0 NormalX=0 NormalY=0 NormalZ=1 AngleXU=0 Radius=1 StartAngle=4.71239 EndAngle=6.28319
    g4: LineSegment StartX=6.08745 StartY=-2.11589 StartZ=0 EndX=7.08745 EndY=-2.11589 EndZ=0
    g5: LineSegment StartX=6.08745 StartY=-4.11588 StartZ=0 EndX=7.08745 EndY=-4.11588 EndZ=0
    g6: ArcOfCircle CenterX=7.08745 CenterY=-1.11589 CenterZ=0 NormalX=0 NormalY=0 NormalZ=1 AngleXU=0 Radius=3 StartAngle=4.71239 EndAngle=6.28319
    g7: ArcOfCircle CenterX=7.08745 CenterY=1.38411 CenterZ=0 NormalX=0 NormalY=0 NormalZ=1 AngleXU=0 Radius=1 StartAngle=5.35e-14 EndAngle=1.5708
    g8: LineSegment StartX=3.58745 StartY=4.38411 StartZ=0 EndX=7.08745 EndY=4.38411 EndZ=0
    g9: LineSegment StartX=10.0875 StartY=-1.11588 StartZ=0 EndX=10.0875 EndY=1.38411 EndZ=0
    g10: ArcOfCircle CenterX=7.08745 CenterY=1.38411 CenterZ=0 NormalX=0 NormalY=0 NormalZ=1 AngleXU=0 Radius=3 StartAngle=3.57e-14 EndAngle=1.5708
    g11: LineSegment StartX=3.58745 StartY=2.38411 StartZ=0 EndX=3.58745 EndY=1.38411 EndZ=0
    g12: ArcOfCircle CenterX=4.58745 CenterY=1.38412 CenterZ=0 NormalX=0 NormalY=0 NormalZ=1 AngleXU=0 Radius=1 StartAngle=1.57081 EndAngle=3.14159
    g13: LineSegment StartX=4.58744 StartY=2.38411 StartZ=0 EndX=7.08745 EndY=2.38411 EndZ=0
  constraints (33):
    c: Vertical(g0)
    c: Vertical(g1)
    c: Distance(g1) = 2
    c: Block(g0)
    c: Block(g2)
    c: Coincident(g3,g2)
    c: Coincident(g4,g0)
    c: Coincident(g4,g3)
    c: Horizontal(g4)
    c: Block(g3)
    c: Coincident(g5,g0)
    c: Horizontal(g5)
    c: Coincident(g6,g3)
    c: Block(g6)
    c: Block(g5)
    c: Coincident(g7,g2)
    c: Block(g7)
    c: Coincident(g8,g1)
    c: Coincident(g9,g6)
    c: Vertical(g9)
    c: Coincident(g10,g7)
    c: Block(g10)
    c: Block(g8)
    c: Block(g9)
    c: Coincident(g11,g1)
    c: Vertical(g11)
    c: Distance(g11) = 1
    c: Coincident(g12,g11)
    c: Coincident(g13,g12)
    c: Coincident(g13,g7)
    c: Horizontal(g13)
    c: Block(g13)
    c: Block(g12)
FEATURE [Sketcher::SketchObject] Sketch044
  FullyConstrained = true
  MapMode = 4
  Placement = pos=(0,0,0) rot=(0.57735,0.57735,0.57735;2.0944rad)
  Support = -> [Cut014]
  sketch-geometry (14):
    g0: LineSegment StartX=6.08745 StartY=-4.11588 StartZ=0 EndX=6.08745 EndY=-2.11589 EndZ=0
    g1: LineSegment StartX=8.08745 StartY=1.38411 StartZ=0 EndX=8.08745 EndY=-1.11589 EndZ=0
    g2: ArcOfCircle CenterX=7.08745 CenterY=-1.11589 CenterZ=0 NormalX=0 NormalY=0 NormalZ=1 AngleXU=0 Radius=1 StartAngle=4.71239 EndAngle=6.28319
    g3: LineSegment StartX=6.08745 StartY=-2.11589 StartZ=0 EndX=7.08745 EndY=-2.11589 EndZ=0
    g4: LineSegment StartX=6.08745 StartY=-4.11588 StartZ=0 EndX=7.08745 EndY=-4.11588 EndZ=0
    g5: ArcOfCircle CenterX=7.08745 CenterY=-1.11589 CenterZ=0 NormalX=0 NormalY=0 NormalZ=1 AngleXU=0 Radius=3 StartAngle=4.71239 EndAngle=6.28319
    g6: ArcOfCircle CenterX=7.08745 CenterY=1.38411 CenterZ=0 NormalX=0 NormalY=0 NormalZ=1 AngleXU=0 Radius=1 StartAngle=5.35e-14 EndAngle=1.5708
    g7: LineSegment StartX=10.0875 StartY=-1.11588 StartZ=0 EndX=10.0875 EndY=1.38411 EndZ=0
    g8: ArcOfCircle CenterX=7.08745 CenterY=1.38411 CenterZ=0 NormalX=0 NormalY=0 NormalZ=1 AngleXU=0 Radius=3 StartAngle=3.57e-14 EndAngle=1.5708
    g9: ArcOfCircle CenterX=4.58745 CenterY=1.38412 CenterZ=0 NormalX=0 NormalY=0 NormalZ=1 AngleXU=0 Radius=1 StartAngle=1.57081 EndAngle=3.14159
    g10: LineSegment StartX=4.58744 StartY=2.38411 StartZ=0 EndX=7.08745 EndY=2.38411 EndZ=0
    g11: LineSegment StartX=4.58745 StartY=4.38411 StartZ=0 EndX=7.08745 EndY=4.38411 EndZ=0
    g12: ArcOfCircle CenterX=4.58745 CenterY=5.38411 CenterZ=0 NormalX=0 NormalY=0 NormalZ=1 AngleXU=0 Radius=1 StartAngle=3.14159 EndAngle=4.71239
    g13: LineSegment StartX=3.58745 StartY=5.38411 StartZ=0 EndX=3.58745 EndY=1.38411 EndZ=0
  constraints (33):
    c: Vertical(g0)
    c: Block(g0)
    c: Block(g1)
    c: Coincident(g2,g1)
    c: Coincident(g3,g0)
    c: Coincident(g3,g2)
    c: Horizontal(g3)
    c: Block(g2)
    c: Coincident(g4,g0)
    c: Horizontal(g4)
    c: Coincident(g5,g2)
    c: Block(g5)
    c: Block(g4)
    c: Coincident(g6,g1)
    c: Block(g6)
    c: Coincident(g7,g5)
    c: Vertical(g7)
    c: Coincident(g8,g6)
    c: Block(g8)
    c: Block(g7)
    c: Coincident(g10,g9)
    c: Coincident(g10,g6)
    c: Horizontal(g10)
    c: Block(g10)
    c: Block(g9)
    c: Coincident(g11,g8)
    c: Horizontal(g11)
    c: Block(g12)
    c: Block(g11)
    c: Coincident(g13,g12)
    c: Coincident(g13,g9)
    c: Vertical(g13)
    c: Tangent(g13,g9)
FEATURE [Part::Extrusion] Extrude039
  Base = -> Sketch044
  Dir = (1,0,0)
  DirMode = 2
  FaceMakerClass = Part::FaceMakerBullseye
  LengthFwd = 10
  LengthRev = 0
  Placement = pos=(8,-22.615,4.115) rot=(0,0,1;3.14159rad)
  Solid = true
  Symmetric = false
FEATURE [App::MeasureDistance] Distance004  label="Distance: 42.16 mm"
  Distance = 42.1607
  P1 = (14.6786,-26.2,1.24491)
  P2 = (-27.4815,-26.2,1.03853)
FEATURE [Sketcher::SketchObject] Sketch045
  FullyConstrained = true
  MapMode = 4
  Placement = pos=(0,0,0) rot=(0.57735,0.57735,0.57735;2.0944rad)
  Support = -> [Cut014]
  sketch-geometry (14):
    g0: LineSegment StartX=6.08745 StartY=-4.11588 StartZ=0 EndX=6.08745 EndY=-2.11589 EndZ=0
    g1: LineSegment StartX=8.08745 StartY=1.38411 StartZ=0 EndX=8.08745 EndY=-1.11589 EndZ=0
    g2: ArcOfCircle CenterX=7.08745 CenterY=-1.11589 CenterZ=0 NormalX=0 NormalY=0 NormalZ=1 AngleXU=0 Radius=1 StartAngle=4.71239 EndAngle=6.28319
    g3: LineSegment StartX=6.08745 StartY=-2.11589 StartZ=0 EndX=7.08745 EndY=-2.11589 EndZ=0
    g4: LineSegment StartX=6.08745 StartY=-4.11588 StartZ=0 EndX=7.08745 EndY=-4.11588 EndZ=0
    g5: ArcOfCircle CenterX=7.08745 CenterY=-1.11589 CenterZ=0 NormalX=0 NormalY=0 NormalZ=1 AngleXU=0 Radius=3 StartAngle=4.71239 EndAngle=6.28319
    g6: ArcOfCircle CenterX=7.08745 CenterY=1.38411 CenterZ=0 NormalX=0 NormalY=0 NormalZ=1 AngleXU=0 Radius=1 StartAngle=5.35e-14 EndAngle=1.5708
    g7: LineSegment StartX=10.0875 StartY=-1.11588 StartZ=0 EndX=10.0875 EndY=1.38411 EndZ=0
    g8: ArcOfCircle CenterX=7.08745 CenterY=1.38411 CenterZ=0 NormalX=0 NormalY=0 NormalZ=1 AngleXU=0 Radius=3 StartAngle=3.57e-14 EndAngle=1.5708
    g9: ArcOfCircle CenterX=4.58745 CenterY=1.38412 CenterZ=0 NormalX=0 NormalY=0 NormalZ=1 AngleXU=0 Radius=1 StartAngle=1.57081 EndAngle=3.14159
    g10: LineSegment StartX=4.58744 StartY=2.38411 StartZ=0 EndX=7.08745 EndY=2.38411 EndZ=0
    g11: LineSegment StartX=4.58745 StartY=4.38411 StartZ=0 EndX=7.08745 EndY=4.38411 EndZ=0
    g12: ArcOfCircle CenterX=4.58745 CenterY=5.38411 CenterZ=0 NormalX=0 NormalY=0 NormalZ=1 AngleXU=0 Radius=1 StartAngle=3.14159 EndAngle=4.71239
    g13: LineSegment StartX=3.58745 StartY=5.38411 StartZ=0 EndX=3.58745 EndY=1.38411 EndZ=0
  constraints (33):
    c: Vertical(g0)
    c: Block(g0)
    c: Block(g1)
    c: Coincident(g2,g1)
    c: Coincident(g3,g0)
    c: Coincident(g3,g2)
    c: Horizontal(g3)
    c: Block(g2)
    c: Coincident(g4,g0)
    c: Horizontal(g4)
    c: Coincident(g5,g2)
    c: Block(g5)
    c: Block(g4)
    c: Coincident(g6,g1)
    c: Block(g6)
    c: Coincident(g7,g5)
    c: Vertical(g7)
    c: Coincident(g8,g6)
    c: Block(g8)
    c: Block(g7)
    c: Coincident(g10,g9)
    c: Coincident(g10,g6)
    c: Horizontal(g10)
    c: Block(g10)
    c: Block(g9)
    c: Coincident(g11,g8)
    c: Horizontal(g11)
    c: Block(g12)
    c: Block(g11)
    c: Coincident(g13,g12)
    c: Coincident(g13,g9)
    c: Vertical(g13)
    c: Tangent(g13,g9)
FEATURE [Part::Extrusion] Extrude040
  Base = -> Sketch045
  Dir = (1,0,0)
  DirMode = 2
  FaceMakerClass = Part::FaceMakerBullseye
  LengthFwd = 10
  LengthRev = 0
  Placement = pos=(-17.5,-22.615,4.115) rot=(0,0,1;3.14159rad)
  Solid = true
  Symmetric = false
FEATURE [Sketcher::SketchObject] Sketch046
  FullyConstrained = true
  MapMode = 4
  Placement = pos=(0,0,0) rot=(0.57735,0.57735,0.57735;2.0944rad)
  Support = -> [Cut014]
  sketch-geometry (14):
    g0: LineSegment StartX=6.08745 StartY=-4.11588 StartZ=0 EndX=6.08745 EndY=-2.11589 EndZ=0
    g1: LineSegment StartX=8.08745 StartY=1.38411 StartZ=0 EndX=8.08745 EndY=-1.11589 EndZ=0
    g2: ArcOfCircle CenterX=7.08745 CenterY=-1.11589 CenterZ=0 NormalX=0 NormalY=0 NormalZ=1 AngleXU=0 Radius=1 StartAngle=4.71239 EndAngle=6.28319
    g3: LineSegment StartX=6.08745 StartY=-2.11589 StartZ=0 EndX=7.08745 EndY=-2.11589 EndZ=0
    g4: LineSegment StartX=6.08745 StartY=-4.11588 StartZ=0 EndX=7.08745 EndY=-4.11588 EndZ=0
    g5: ArcOfCircle CenterX=7.08745 CenterY=-1.11589 CenterZ=0 NormalX=0 NormalY=0 NormalZ=1 AngleXU=0 Radius=3 StartAngle=4.71239 EndAngle=6.28319
    g6: ArcOfCircle CenterX=7.08745 CenterY=1.38411 CenterZ=0 NormalX=0 NormalY=0 NormalZ=1 AngleXU=0 Radius=1 StartAngle=5.35e-14 EndAngle=1.5708
    g7: LineSegment StartX=10.0875 StartY=-1.11588 StartZ=0 EndX=10.0875 EndY=1.38411 EndZ=0
    g8: ArcOfCircle CenterX=7.08745 CenterY=1.38411 CenterZ=0 NormalX=0 NormalY=0 NormalZ=1 AngleXU=0 Radius=3 StartAngle=3.57e-14 EndAngle=1.5708
    g9: ArcOfCircle CenterX=4.58745 CenterY=1.38412 CenterZ=0 NormalX=0 NormalY=0 NormalZ=1 AngleXU=0 Radius=1 StartAngle=1.57081 EndAngle=3.14159
    g10: LineSegment StartX=4.58744 StartY=2.38411 StartZ=0 EndX=7.08745 EndY=2.38411 EndZ=0
    g11: LineSegment StartX=4.58745 StartY=4.38411 StartZ=0 EndX=7.08745 EndY=4.38411 EndZ=0
    g12: ArcOfCircle CenterX=4.58745 CenterY=5.38411 CenterZ=0 NormalX=0 NormalY=0 NormalZ=1 AngleXU=0 Radius=1 StartAngle=3.14159 EndAngle=4.71239
    g13: LineSegment StartX=3.58745 StartY=5.38411 StartZ=0 EndX=3.58745 EndY=1.38411 EndZ=0
  constraints (33):
    c: Vertical(g0)
    c: Block(g0)
    c: Block(g1)
    c: Coincident(g2,g1)
    c: Coincident(g3,g0)
    c: Coincident(g3,g2)
    c: Horizontal(g3)
    c: Block(g2)
    c: Coincident(g4,g0)
    c: Horizontal(g4)
    c: Coincident(g5,g2)
    c: Block(g5)
    c: Block(g4)
    c: Coincident(g6,g1)
    c: Block(g6)
    c: Coincident(g7,g5)
    c: Vertical(g7)
    c: Coincident(g8,g6)
    c: Block(g8)
    c: Block(g7)
    c: Coincident(g10,g9)
    c: Coincident(g10,g6)
    c: Horizontal(g10)
    c: Block(g10)
    c: Block(g9)
    c: Coincident(g11,g8)
    c: Horizontal(g11)
    c: Block(g12)
    c: Block(g11)
    c: Coincident(g13,g12)
    c: Coincident(g13,g9)
    c: Vertical(g13)
    c: Tangent(g13,g9)
FEATURE [Sketcher::SketchObject] Sketch047
  FullyConstrained = true
  MapMode = 4
  Placement = pos=(0,0,0) rot=(0.57735,0.57735,0.57735;2.0944rad)
  Support = -> [Cut014]
  sketch-geometry (14):
    g0: LineSegment StartX=6.08745 StartY=-4.11588 StartZ=0 EndX=6.08745 EndY=-2.11589 EndZ=0
    g1: LineSegment StartX=8.08745 StartY=1.38411 StartZ=0 EndX=8.08745 EndY=-1.11589 EndZ=0
    g2: ArcOfCircle CenterX=7.08745 CenterY=-1.11589 CenterZ=0 NormalX=0 NormalY=0 NormalZ=1 AngleXU=0 Radius=1 StartAngle=4.71239 EndAngle=6.28319
    g3: LineSegment StartX=6.08745 StartY=-2.11589 StartZ=0 EndX=7.08745 EndY=-2.11589 EndZ=0
    g4: LineSegment StartX=6.08745 StartY=-4.11588 StartZ=0 EndX=7.08745 EndY=-4.11588 EndZ=0
    g5: ArcOfCircle CenterX=7.08745 CenterY=-1.11589 CenterZ=0 NormalX=0 NormalY=0 NormalZ=1 AngleXU=0 Radius=3 StartAngle=4.71239 EndAngle=6.28319
    g6: ArcOfCircle CenterX=7.08745 CenterY=1.38411 CenterZ=0 NormalX=0 NormalY=0 NormalZ=1 AngleXU=0 Radius=1 StartAngle=5.35e-14 EndAngle=1.5708
    g7: LineSegment StartX=10.0875 StartY=-1.11588 StartZ=0 EndX=10.0875 EndY=1.38411 EndZ=0
    g8: ArcOfCircle CenterX=7.08745 CenterY=1.38411 CenterZ=0 NormalX=0 NormalY=0 NormalZ=1 AngleXU=0 Radius=3 StartAngle=3.57e-14 EndAngle=1.5708
    g9: ArcOfCircle CenterX=4.58745 CenterY=1.38412 CenterZ=0 NormalX=0 NormalY=0 NormalZ=1 AngleXU=0 Radius=1 StartAngle=1.57081 EndAngle=3.14159
    g10: LineSegment StartX=4.58744 StartY=2.38411 StartZ=0 EndX=7.08745 EndY=2.38411 EndZ=0
    g11: LineSegment StartX=4.58745 StartY=4.38411 StartZ=0 EndX=7.08745 EndY=4.38411 EndZ=0
    g12: ArcOfCircle CenterX=4.58745 CenterY=5.38411 CenterZ=0 NormalX=0 NormalY=0 NormalZ=1 AngleXU=0 Radius=1 StartAngle=3.14159 EndAngle=4.71239
    g13: LineSegment StartX=3.58745 StartY=5.38411 StartZ=0 EndX=3.58745 EndY=1.38411 EndZ=0
  constraints (33):
    c: Vertical(g0)
    c: Block(g0)
    c: Block(g1)
    c: Coincident(g2,g1)
    c: Coincident(g3,g0)
    c: Coincident(g3,g2)
    c: Horizontal(g3)
    c: Block(g2)
    c: Coincident(g4,g0)
    c: Horizontal(g4)
    c: Coincident(g5,g2)
    c: Block(g5)
    c: Block(g4)
    c: Coincident(g6,g1)
    c: Block(g6)
    c: Coincident(g7,g5)
    c: Vertical(g7)
    c: Coincident(g8,g6)
    c: Block(g8)
    c: Block(g7)
    c: Coincident(g10,g9)
    c: Coincident(g10,g6)
    c: Horizontal(g10)
    c: Block(g10)
    c: Block(g9)
    c: Coincident(g11,g8)
    c: Horizontal(g11)
    c: Block(g12)
    c: Block(g11)
    c: Coincident(g13,g12)
    c: Coincident(g13,g9)
    c: Vertical(g13)
    c: Tangent(g13,g9)
FEATURE [Sketcher::SketchObject] Sketch048
  FullyConstrained = true
  MapMode = 4
  Placement = pos=(0,0,0) rot=(0.57735,0.57735,0.57735;2.0944rad)
  Support = -> [Cut014]
  sketch-geometry (14):
    g0: LineSegment StartX=6.08745 StartY=-4.11588 StartZ=0 EndX=6.08745 EndY=-2.11589 EndZ=0
    g1: LineSegment StartX=8.08745 StartY=1.38411 StartZ=0 EndX=8.08745 EndY=-1.11589 EndZ=0
    g2: ArcOfCircle CenterX=7.08745 CenterY=-1.11589 CenterZ=0 NormalX=0 NormalY=0 NormalZ=1 AngleXU=0 Radius=1 StartAngle=4.71239 EndAngle=6.28319
    g3: LineSegment StartX=6.08745 StartY=-2.11589 StartZ=0 EndX=7.08745 EndY=-2.11589 EndZ=0
    g4: LineSegment StartX=6.08745 StartY=-4.11588 StartZ=0 EndX=7.08745 EndY=-4.11588 EndZ=0
    g5: ArcOfCircle CenterX=7.08745 CenterY=-1.11589 CenterZ=0 NormalX=0 NormalY=0 NormalZ=1 AngleXU=0 Radius=3 StartAngle=4.71239 EndAngle=6.28319
    g6: ArcOfCircle CenterX=7.08745 CenterY=1.38411 CenterZ=0 NormalX=0 NormalY=0 NormalZ=1 AngleXU=0 Radius=1 StartAngle=5.35e-14 EndAngle=1.5708
    g7: LineSegment StartX=10.0875 StartY=-1.11588 StartZ=0 EndX=10.0875 EndY=1.38411 EndZ=0
    g8: ArcOfCircle CenterX=7.08745 CenterY=1.38411 CenterZ=0 NormalX=0 NormalY=0 NormalZ=1 AngleXU=0 Radius=3 StartAngle=3.57e-14 EndAngle=1.5708
    g9: ArcOfCircle CenterX=4.58745 CenterY=1.38412 CenterZ=0 NormalX=0 NormalY=0 NormalZ=1 AngleXU=0 Radius=1 StartAngle=1.57081 EndAngle=3.14159
    g10: LineSegment StartX=4.58744 StartY=2.38411 StartZ=0 EndX=7.08745 EndY=2.38411 EndZ=0
    g11: LineSegment StartX=4.58745 StartY=4.38411 StartZ=0 EndX=7.08745 EndY=4.38411 EndZ=0
    g12: ArcOfCircle CenterX=4.58745 CenterY=5.38411 CenterZ=0 NormalX=0 NormalY=0 NormalZ=1 AngleXU=0 Radius=1 StartAngle=3.14159 EndAngle=4.71239
    g13: LineSegment StartX=3.58745 StartY=5.38411 StartZ=0 EndX=3.58745 EndY=1.38411 EndZ=0
  constraints (33):
    c: Vertical(g0)
    c: Block(g0)
    c: Block(g1)
    c: Coincident(g2,g1)
    c: Coincident(g3,g0)
    c: Coincident(g3,g2)
    c: Horizontal(g3)
    c: Block(g2)
    c: Coincident(g4,g0)
    c: Horizontal(g4)
    c: Coincident(g5,g2)
    c: Block(g5)
    c: Block(g4)
    c: Coincident(g6,g1)
    c: Block(g6)
    c: Coincident(g7,g5)
    c: Vertical(g7)
    c: Coincident(g8,g6)
    c: Block(g8)
    c: Block(g7)
    c: Coincident(g10,g9)
    c: Coincident(g10,g6)
    c: Horizontal(g10)
    c: Block(g10)
    c: Block(g9)
    c: Coincident(g11,g8)
    c: Horizontal(g11)
    c: Block(g12)
    c: Block(g11)
    c: Coincident(g13,g12)
    c: Coincident(g13,g9)
    c: Vertical(g13)
    c: Tangent(g13,g9)
FEATURE [Sketcher::SketchObject] Sketch049
  FullyConstrained = true
  MapMode = 4
  Placement = pos=(0,0,0) rot=(0.57735,0.57735,0.57735;2.0944rad)
  Support = -> [Cut014]
  sketch-geometry (14):
    g0: LineSegment StartX=6.08745 StartY=-4.11588 StartZ=0 EndX=6.08745 EndY=-2.11589 EndZ=0
    g1: LineSegment StartX=8.08745 StartY=1.38411 StartZ=0 EndX=8.08745 EndY=-1.11589 EndZ=0
    g2: ArcOfCircle CenterX=7.08745 CenterY=-1.11589 CenterZ=0 NormalX=0 NormalY=0 NormalZ=1 AngleXU=0 Radius=1 StartAngle=4.71239 EndAngle=6.28319
    g3: LineSegment StartX=6.08745 StartY=-2.11589 StartZ=0 EndX=7.08745 EndY=-2.11589 EndZ=0
    g4: LineSegment StartX=6.08745 StartY=-4.11588 StartZ=0 EndX=7.08745 EndY=-4.11588 EndZ=0
    g5: ArcOfCircle CenterX=7.08745 CenterY=-1.11589 CenterZ=0 NormalX=0 NormalY=0 NormalZ=1 AngleXU=0 Radius=3 StartAngle=4.71239 EndAngle=6.28319
    g6: ArcOfCircle CenterX=7.08745 CenterY=1.38411 CenterZ=0 NormalX=0 NormalY=0 NormalZ=1 AngleXU=0 Radius=1 StartAngle=5.35e-14 EndAngle=1.5708
    g7: LineSegment StartX=10.0875 StartY=-1.11588 StartZ=0 EndX=10.0875 EndY=1.38411 EndZ=0
    g8: ArcOfCircle CenterX=7.08745 CenterY=1.38411 CenterZ=0 NormalX=0 NormalY=0 NormalZ=1 AngleXU=0 Radius=3 StartAngle=3.57e-14 EndAngle=1.5708
    g9: ArcOfCircle CenterX=4.58745 CenterY=1.38412 CenterZ=0 NormalX=0 NormalY=0 NormalZ=1 AngleXU=0 Radius=1 StartAngle=1.57081 EndAngle=3.14159
    g10: LineSegment StartX=4.58744 StartY=2.38411 StartZ=0 EndX=7.08745 EndY=2.38411 EndZ=0
    g11: LineSegment StartX=4.58745 StartY=4.38411 StartZ=0 EndX=7.08745 EndY=4.38411 EndZ=0
    g12: ArcOfCircle CenterX=4.58745 CenterY=5.38411 CenterZ=0 NormalX=0 NormalY=0 NormalZ=1 AngleXU=0 Radius=1 StartAngle=3.14159 EndAngle=4.71239
    g13: LineSegment StartX=3.58745 StartY=5.38411 StartZ=0 EndX=3.58745 EndY=1.38411 EndZ=0
  constraints (33):
    c: Vertical(g0)
    c: Block(g0)
    c: Block(g1)
    c: Coincident(g2,g1)
    c: Coincident(g3,g0)
    c: Coincident(g3,g2)
    c: Horizontal(g3)
    c: Block(g2)
    c: Coincident(g4,g0)
    c: Horizontal(g4)
    c: Coincident(g5,g2)
    c: Block(g5)
    c: Block(g4)
    c: Coincident(g6,g1)
    c: Block(g6)
    c: Coincident(g7,g5)
    c: Vertical(g7)
    c: Coincident(g8,g6)
    c: Block(g8)
    c: Block(g7)
    c: Coincident(g10,g9)
    c: Coincident(g10,g6)
    c: Horizontal(g10)
    c: Block(g10)
    c: Block(g9)
    c: Coincident(g11,g8)
    c: Horizontal(g11)
    c: Block(g12)
    c: Block(g11)
    c: Coincident(g13,g12)
    c: Coincident(g13,g9)
    c: Vertical(g13)
    c: Tangent(g13,g9)
FEATURE [Part::Extrusion] Extrude041
  Base = -> Sketch049
  Dir = (1,0,0)
  DirMode = 2
  FaceMakerClass = Part::FaceMakerBullseye
  LengthFwd = 10
  LengthRev = 0
  Placement = pos=(-2,-22.615,14.6) rot=(0,0,1;3.14159rad)
  Solid = true
  Symmetric = false
FEATURE [Part::MultiFuse] Fusion023
  Shapes = -> [Extrude039,Extrude040,Extrude041,Cut014,Fusion015]
FEATURE [Part::Extrusion] Extrude042
  Base = -> Sketch034
  Dir = (0,0.894389,-0.447291)
  DirMode = 2
  FaceMakerClass = Part::FaceMakerBullseye
  LengthFwd = 14
  LengthRev = 0
  Placement = pos=(45.5,-14,11) rot=(1,0,0;0.466003rad)
  Solid = true
  Symmetric = false
FEATURE [Part::Fillet] Fillet021
  Base = -> Extrude042
  Edges = 1 edges r=1.95: [Edge2]
FEATURE [Part::Fillet] Fillet022
  Base = -> Fillet021
  Edges = 1 edges r=1.9: [Edge12]
FEATURE [Part::Box] Box014  label="Cube014"
  AttacherType = Attacher::AttachEngine3D
  Height = 2
  Length = 2
  Placement = pos=(-12.85,-28.2,0) rot=(0,0,1;0rad)
  Width = 2
FEATURE [App::MeasureDistance] Distance005  label="Distance: 15.50 mm"
  Distance = 15.5
  P1 = (-17.5,-32.7025,2.99911)
  P2 = (-2,-32.7025,2.99911)
FEATURE [Part::Box] Box015  label="Cube015"
  AttacherType = Attacher::AttachEngine3D
  Height = 2
  Length = 2
  Placement = pos=(-10.85,-28.2,0) rot=(0,0,1;0rad)
  Width = 2
FEATURE [Part::MultiFuse] Fusion024
  Shapes = -> [Box015,Box014]
